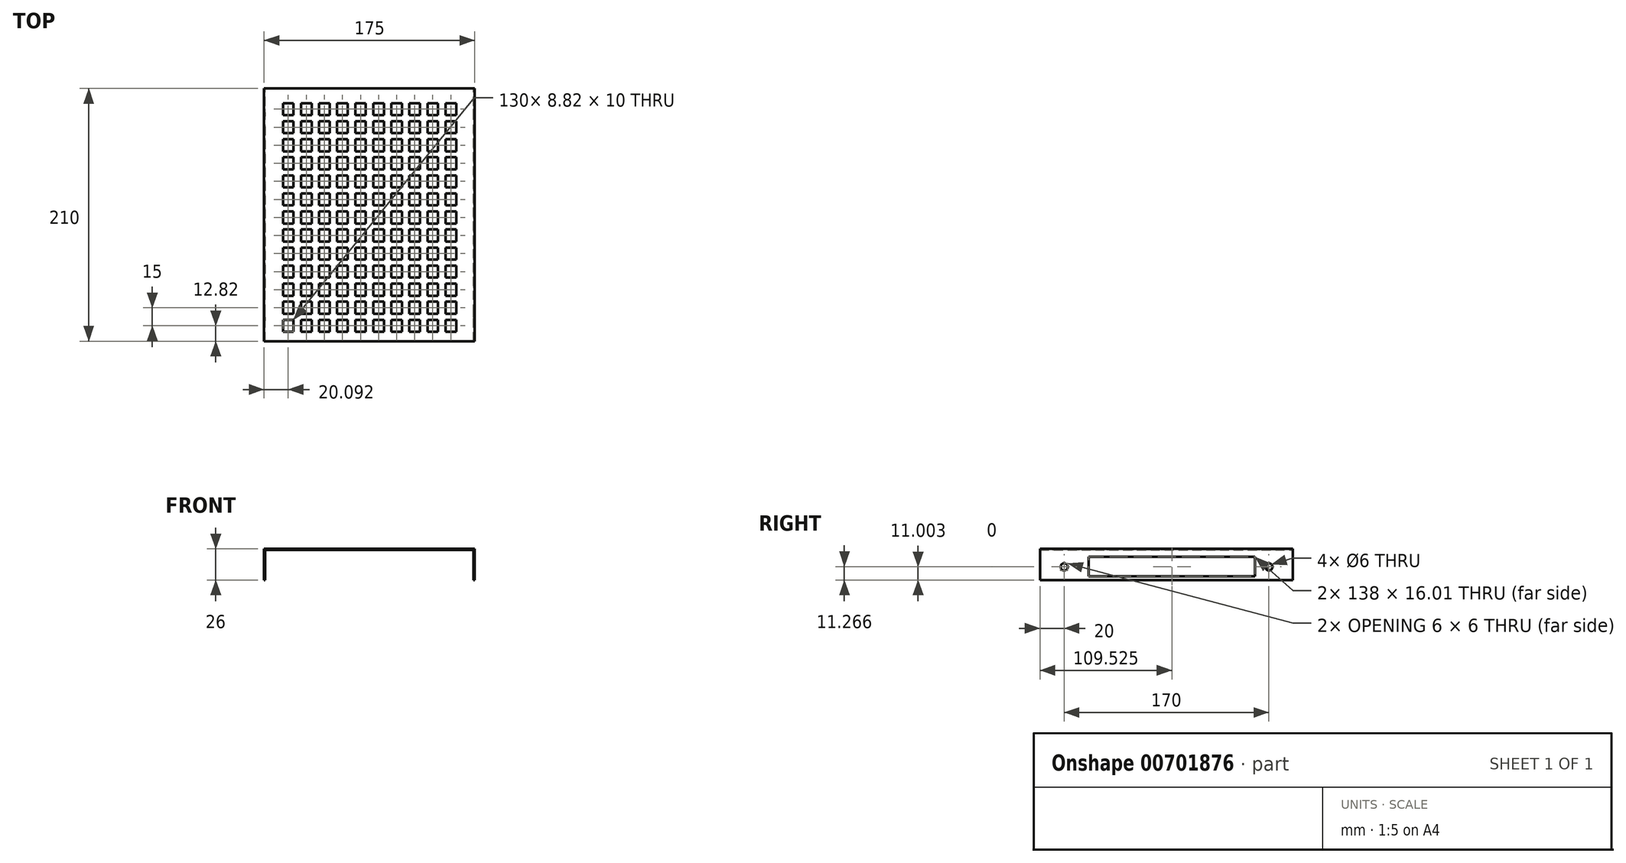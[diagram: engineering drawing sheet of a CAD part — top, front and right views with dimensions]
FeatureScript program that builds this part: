
annotation { "Feature Type Name" : "Feature", "Feature Type Description" : "" }
export const myFeature = defineFeature(function(context is Context, id is Id, definition is map)
    precondition{}
    {
        {
            var Q0;
            Q0=qCreatedBy(makeId("Front.planeOp"),FACE);
            var sketch = newSketch(context, id + "F0", { "sketchPlane" : qUnion([Q0])});
            skLineSegment(sketch, "E0", {"start": v(-108.9, 51.33) * mm, "end": v(66.1, 51.33) * mm});
            skLineSegment(sketch, "E1", {"start": v(-108.9, 51.33) * mm, "end": v(-108.9, 25.33) * mm});
            skLineSegment(sketch, "E2", {"start": v(-108.9, 25.33) * mm, "end": v(-107.9, 25.33) * mm});
            skLineSegment(sketch, "E3", {"start": v(-107.9, 25.33) * mm, "end": v(-107.9, 50.33) * mm});
            skLineSegment(sketch, "E4", {"start": v(66.1, 51.33) * mm, "end": v(66.1, 25.33) * mm});
            skLineSegment(sketch, "E5", {"start": v(66.1, 25.33) * mm, "end": v(65.1, 25.33) * mm});
            skLineSegment(sketch, "E6", {"start": v(65.1, 25.33) * mm, "end": v(65.1, 50.33) * mm});
            skLineSegment(sketch, "E7", {"start": v(65.1, 50.33) * mm, "end": v(-107.9, 50.33) * mm});
            skSolve(sketch);
        }
        {
            var Q0;
            Q0=qSketchRegion(id+"F0",true);
            extrude(context, id + "F1", {"entities" : qUnion([Q0]), "depth" : 210 * mm, "offsetDistance" : 25 * mm});
        }
        {
            var Q0;
            Q0=makeQuery(id+"F1.opExtrude","SWEPT_FACE",FACE,{"disambiguationData":[OSD([sQuery(id+"F0.wireOp",EDGE,"E4")])]});
            var sketch = newSketch(context, id + "F2", { "sketchPlane" : qUnion([Q0])});
            skCircle(sketch, "E8", {"center": v(-190, 36.33) * mm, "radius": 3 * mm});
            skCircle(sketch, "E9", {"center": v(-20, 36.33) * mm, "radius": 3 * mm});
            skSolve(sketch);
        }
        {
            var Q0;
            Q0=sQuery(id+"F2.wireOp",VERTEX,"E8.center");
            var Q1;
            Q1=makeQuery(id+"F1.opExtrude","SWEPT_BODY",BODY,{"disambiguationData":[OSD([sQuery(id+"F0.wireOp",EDGE,"E0"),sQuery(id+"F0.wireOp",EDGE,"E1"),sQuery(id+"F0.wireOp",EDGE,"E2"),sQuery(id+"F0.wireOp",EDGE,"E3"),sQuery(id+"F0.wireOp",EDGE,"E4"),sQuery(id+"F0.wireOp",EDGE,"E5"),sQuery(id+"F0.wireOp",EDGE,"E6"),sQuery(id+"F0.wireOp",EDGE,"E7")])]});
            hole(context, id + "F3", {"style" : HoleStyle.SIMPLE, "endStyle" : HoleEndStyle.THROUGH, "holeDiameter" : 6 * mm, "majorDiameter" : 5 * mm, "isTappedThrough" : true, "tappedDepth" : 12 * mm, "tapClearance" : 3, "locations" : qUnion([Q0]), "scope" : qUnion([Q1])});
        }
        {
            var Q0;
            Q0=sQuery(id+"F2.wireOp",VERTEX,"E9.center");
            var Q1;
            Q1=makeQuery(id+"F1.opExtrude","SWEPT_BODY",BODY,{"disambiguationData":[OSD([sQuery(id+"F0.wireOp",EDGE,"E0"),sQuery(id+"F0.wireOp",EDGE,"E1"),sQuery(id+"F0.wireOp",EDGE,"E2"),sQuery(id+"F0.wireOp",EDGE,"E3"),sQuery(id+"F0.wireOp",EDGE,"E4"),sQuery(id+"F0.wireOp",EDGE,"E5"),sQuery(id+"F0.wireOp",EDGE,"E6"),sQuery(id+"F0.wireOp",EDGE,"E7")])]});
            hole(context, id + "F4", {"style" : HoleStyle.SIMPLE, "endStyle" : HoleEndStyle.THROUGH, "holeDiameter" : 6 * mm, "majorDiameter" : 5 * mm, "isTappedThrough" : true, "tappedDepth" : 12 * mm, "tapClearance" : 3, "locations" : qUnion([Q0]), "scope" : qUnion([Q1])});
        }
        {
            var Q0;
            Q0=qCreatedBy(makeId("Right.planeOp"),FACE);
            var sketch = newSketch(context, id + "F5", { "sketchPlane" : qUnion([Q0])});
            skLineSegment(sketch, "E10.bottom", {"start": v(-169.47, 44.6) * mm, "end": v(-31.48, 44.6) * mm});
            skLineSegment(sketch, "E10.top", {"start": v(-169.47, 28.6) * mm, "end": v(-31.48, 28.6) * mm});
            skLineSegment(sketch, "E10.left", {"start": v(-169.47, 44.6) * mm, "end": v(-169.47, 28.6) * mm});
            skLineSegment(sketch, "E10.right", {"start": v(-31.48, 44.6) * mm, "end": v(-31.48, 28.6) * mm});
            skPoint(sketch, "E10.middle", {"position": v(-100.47, 36.6) * mm});
            skSolve(sketch);
        }
        {
            var Q0;
            Q0=makeQuery(id+"F5.imprint","IMPRINT",FACE,{"disambiguationData":[TD([[makeQuery(id+"F5.imprint","IMPRINT",EDGE,{"derivedFrom":sQuery(id+"F5.wireOp",EDGE,"E10.bottom")}),-1.0]])]});
            extrude(context, id + "F6", {"entities" : qUnion([Q0]), "operationType" : NewBodyOperationType.REMOVE, "endBound" : BoundingType.SYMMETRIC, "oppositeDirection" : true, "depth" : 300 * mm, "offsetDistance" : 25 * mm});
        }
        {
            var Q0;
            Q0=makeQuery(id+"F1.opExtrude","SWEPT_FACE",FACE,{"disambiguationData":[OSD([sQuery(id+"F0.wireOp",EDGE,"E0")])]});
            var sketch = newSketch(context, id + "F7", { "sketchPlane" : qUnion([Q0])});
            skLineSegment(sketch, "E11.bottom", {"start": v(-93.22, -12.18) * mm, "end": v(-84.4, -12.18) * mm});
            skLineSegment(sketch, "E11.top", {"start": v(-93.22, -22.18) * mm, "end": v(-84.4, -22.18) * mm});
            skLineSegment(sketch, "E11.left", {"start": v(-93.22, -12.18) * mm, "end": v(-93.22, -22.18) * mm});
            skLineSegment(sketch, "E11.right", {"start": v(-84.4, -12.18) * mm, "end": v(-84.4, -22.18) * mm});
            skLineSegment(sketch, "E12.0.1.0", {"start": v(-84.4, -27.18) * mm, "end": v(-84.4, -37.18) * mm});
            skLineSegment(sketch, "E12.0.1.1", {"start": v(-93.22, -27.18) * mm, "end": v(-84.4, -27.18) * mm});
            skLineSegment(sketch, "E12.0.1.2", {"start": v(-93.22, -37.18) * mm, "end": v(-84.4, -37.18) * mm});
            skLineSegment(sketch, "E12.0.1.3", {"start": v(-93.22, -27.18) * mm, "end": v(-93.22, -37.18) * mm});
            skLineSegment(sketch, "E12.0.2.0", {"start": v(-84.4, -42.18) * mm, "end": v(-84.4, -52.18) * mm});
            skLineSegment(sketch, "E12.0.2.1", {"start": v(-93.22, -42.18) * mm, "end": v(-84.4, -42.18) * mm});
            skLineSegment(sketch, "E12.0.2.2", {"start": v(-93.22, -52.18) * mm, "end": v(-84.4, -52.18) * mm});
            skLineSegment(sketch, "E12.0.2.3", {"start": v(-93.22, -42.18) * mm, "end": v(-93.22, -52.18) * mm});
            skLineSegment(sketch, "E12.0.3.0", {"start": v(-84.4, -57.18) * mm, "end": v(-84.4, -67.18) * mm});
            skLineSegment(sketch, "E12.0.3.1", {"start": v(-93.22, -57.18) * mm, "end": v(-84.4, -57.18) * mm});
            skLineSegment(sketch, "E12.0.3.2", {"start": v(-93.22, -67.18) * mm, "end": v(-84.4, -67.18) * mm});
            skLineSegment(sketch, "E12.0.3.3", {"start": v(-93.22, -57.18) * mm, "end": v(-93.22, -67.18) * mm});
            skLineSegment(sketch, "E12.0.4.0", {"start": v(-84.4, -72.18) * mm, "end": v(-84.4, -82.18) * mm});
            skLineSegment(sketch, "E12.0.4.1", {"start": v(-93.22, -72.18) * mm, "end": v(-84.4, -72.18) * mm});
            skLineSegment(sketch, "E12.0.4.2", {"start": v(-93.22, -82.18) * mm, "end": v(-84.4, -82.18) * mm});
            skLineSegment(sketch, "E12.0.4.3", {"start": v(-93.22, -72.18) * mm, "end": v(-93.22, -82.18) * mm});
            skLineSegment(sketch, "E12.0.5.0", {"start": v(-84.4, -87.18) * mm, "end": v(-84.4, -97.18) * mm});
            skLineSegment(sketch, "E12.0.5.1", {"start": v(-93.22, -87.18) * mm, "end": v(-84.4, -87.18) * mm});
            skLineSegment(sketch, "E12.0.5.2", {"start": v(-93.22, -97.18) * mm, "end": v(-84.4, -97.18) * mm});
            skLineSegment(sketch, "E12.0.5.3", {"start": v(-93.22, -87.18) * mm, "end": v(-93.22, -97.18) * mm});
            skLineSegment(sketch, "E12.0.6.0", {"start": v(-84.4, -102.18) * mm, "end": v(-84.4, -112.18) * mm});
            skLineSegment(sketch, "E12.0.6.1", {"start": v(-93.22, -102.18) * mm, "end": v(-84.4, -102.18) * mm});
            skLineSegment(sketch, "E12.0.6.2", {"start": v(-93.22, -112.18) * mm, "end": v(-84.4, -112.18) * mm});
            skLineSegment(sketch, "E12.0.6.3", {"start": v(-93.22, -102.18) * mm, "end": v(-93.22, -112.18) * mm});
            skLineSegment(sketch, "E12.0.7.0", {"start": v(-84.4, -117.18) * mm, "end": v(-84.4, -127.18) * mm});
            skLineSegment(sketch, "E12.0.7.1", {"start": v(-93.22, -117.18) * mm, "end": v(-84.4, -117.18) * mm});
            skLineSegment(sketch, "E12.0.7.2", {"start": v(-93.22, -127.18) * mm, "end": v(-84.4, -127.18) * mm});
            skLineSegment(sketch, "E12.0.7.3", {"start": v(-93.22, -117.18) * mm, "end": v(-93.22, -127.18) * mm});
            skLineSegment(sketch, "E12.0.8.0", {"start": v(-84.4, -132.18) * mm, "end": v(-84.4, -142.18) * mm});
            skLineSegment(sketch, "E12.0.8.1", {"start": v(-93.22, -132.18) * mm, "end": v(-84.4, -132.18) * mm});
            skLineSegment(sketch, "E12.0.8.2", {"start": v(-93.22, -142.18) * mm, "end": v(-84.4, -142.18) * mm});
            skLineSegment(sketch, "E12.0.8.3", {"start": v(-93.22, -132.18) * mm, "end": v(-93.22, -142.18) * mm});
            skLineSegment(sketch, "E12.0.9.0", {"start": v(-84.4, -147.18) * mm, "end": v(-84.4, -157.18) * mm});
            skLineSegment(sketch, "E12.0.9.1", {"start": v(-93.22, -147.18) * mm, "end": v(-84.4, -147.18) * mm});
            skLineSegment(sketch, "E12.0.9.2", {"start": v(-93.22, -157.18) * mm, "end": v(-84.4, -157.18) * mm});
            skLineSegment(sketch, "E12.0.9.3", {"start": v(-93.22, -147.18) * mm, "end": v(-93.22, -157.18) * mm});
            skLineSegment(sketch, "E12.1.0.0", {"start": v(-69.4, -12.18) * mm, "end": v(-69.4, -22.18) * mm});
            skLineSegment(sketch, "E12.1.0.1", {"start": v(-78.22, -12.18) * mm, "end": v(-69.4, -12.18) * mm});
            skLineSegment(sketch, "E12.1.0.2", {"start": v(-78.22, -22.18) * mm, "end": v(-69.4, -22.18) * mm});
            skLineSegment(sketch, "E12.1.0.3", {"start": v(-78.22, -12.18) * mm, "end": v(-78.22, -22.18) * mm});
            skLineSegment(sketch, "E12.1.1.0", {"start": v(-69.4, -27.18) * mm, "end": v(-69.4, -37.18) * mm});
            skLineSegment(sketch, "E12.1.1.1", {"start": v(-78.22, -27.18) * mm, "end": v(-69.4, -27.18) * mm});
            skLineSegment(sketch, "E12.1.1.2", {"start": v(-78.22, -37.18) * mm, "end": v(-69.4, -37.18) * mm});
            skLineSegment(sketch, "E12.1.1.3", {"start": v(-78.22, -27.18) * mm, "end": v(-78.22, -37.18) * mm});
            skLineSegment(sketch, "E12.1.2.0", {"start": v(-69.4, -42.18) * mm, "end": v(-69.4, -52.18) * mm});
            skLineSegment(sketch, "E12.1.2.1", {"start": v(-78.22, -42.18) * mm, "end": v(-69.4, -42.18) * mm});
            skLineSegment(sketch, "E12.1.2.2", {"start": v(-78.22, -52.18) * mm, "end": v(-69.4, -52.18) * mm});
            skLineSegment(sketch, "E12.1.2.3", {"start": v(-78.22, -42.18) * mm, "end": v(-78.22, -52.18) * mm});
            skLineSegment(sketch, "E12.1.3.0", {"start": v(-69.4, -57.18) * mm, "end": v(-69.4, -67.18) * mm});
            skLineSegment(sketch, "E12.1.3.1", {"start": v(-78.22, -57.18) * mm, "end": v(-69.4, -57.18) * mm});
            skLineSegment(sketch, "E12.1.3.2", {"start": v(-78.22, -67.18) * mm, "end": v(-69.4, -67.18) * mm});
            skLineSegment(sketch, "E12.1.3.3", {"start": v(-78.22, -57.18) * mm, "end": v(-78.22, -67.18) * mm});
            skLineSegment(sketch, "E12.1.4.0", {"start": v(-69.4, -72.18) * mm, "end": v(-69.4, -82.18) * mm});
            skLineSegment(sketch, "E12.1.4.1", {"start": v(-78.22, -72.18) * mm, "end": v(-69.4, -72.18) * mm});
            skLineSegment(sketch, "E12.1.4.2", {"start": v(-78.22, -82.18) * mm, "end": v(-69.4, -82.18) * mm});
            skLineSegment(sketch, "E12.1.4.3", {"start": v(-78.22, -72.18) * mm, "end": v(-78.22, -82.18) * mm});
            skLineSegment(sketch, "E12.1.5.0", {"start": v(-69.4, -87.18) * mm, "end": v(-69.4, -97.18) * mm});
            skLineSegment(sketch, "E12.1.5.1", {"start": v(-78.22, -87.18) * mm, "end": v(-69.4, -87.18) * mm});
            skLineSegment(sketch, "E12.1.5.2", {"start": v(-78.22, -97.18) * mm, "end": v(-69.4, -97.18) * mm});
            skLineSegment(sketch, "E12.1.5.3", {"start": v(-78.22, -87.18) * mm, "end": v(-78.22, -97.18) * mm});
            skLineSegment(sketch, "E12.1.6.0", {"start": v(-69.4, -102.18) * mm, "end": v(-69.4, -112.18) * mm});
            skLineSegment(sketch, "E12.1.6.1", {"start": v(-78.22, -102.18) * mm, "end": v(-69.4, -102.18) * mm});
            skLineSegment(sketch, "E12.1.6.2", {"start": v(-78.22, -112.18) * mm, "end": v(-69.4, -112.18) * mm});
            skLineSegment(sketch, "E12.1.6.3", {"start": v(-78.22, -102.18) * mm, "end": v(-78.22, -112.18) * mm});
            skLineSegment(sketch, "E12.1.7.0", {"start": v(-69.4, -117.18) * mm, "end": v(-69.4, -127.18) * mm});
            skLineSegment(sketch, "E12.1.7.1", {"start": v(-78.22, -117.18) * mm, "end": v(-69.4, -117.18) * mm});
            skLineSegment(sketch, "E12.1.7.2", {"start": v(-78.22, -127.18) * mm, "end": v(-69.4, -127.18) * mm});
            skLineSegment(sketch, "E12.1.7.3", {"start": v(-78.22, -117.18) * mm, "end": v(-78.22, -127.18) * mm});
            skLineSegment(sketch, "E12.1.8.0", {"start": v(-69.4, -132.18) * mm, "end": v(-69.4, -142.18) * mm});
            skLineSegment(sketch, "E12.1.8.1", {"start": v(-78.22, -132.18) * mm, "end": v(-69.4, -132.18) * mm});
            skLineSegment(sketch, "E12.1.8.2", {"start": v(-78.22, -142.18) * mm, "end": v(-69.4, -142.18) * mm});
            skLineSegment(sketch, "E12.1.8.3", {"start": v(-78.22, -132.18) * mm, "end": v(-78.22, -142.18) * mm});
            skLineSegment(sketch, "E12.1.9.0", {"start": v(-69.4, -147.18) * mm, "end": v(-69.4, -157.18) * mm});
            skLineSegment(sketch, "E12.1.9.1", {"start": v(-78.22, -147.18) * mm, "end": v(-69.4, -147.18) * mm});
            skLineSegment(sketch, "E12.1.9.2", {"start": v(-78.22, -157.18) * mm, "end": v(-69.4, -157.18) * mm});
            skLineSegment(sketch, "E12.1.9.3", {"start": v(-78.22, -147.18) * mm, "end": v(-78.22, -157.18) * mm});
            skLineSegment(sketch, "E12.2.0.0", {"start": v(-54.4, -12.18) * mm, "end": v(-54.4, -22.18) * mm});
            skLineSegment(sketch, "E12.2.0.1", {"start": v(-63.22, -12.18) * mm, "end": v(-54.4, -12.18) * mm});
            skLineSegment(sketch, "E12.2.0.2", {"start": v(-63.22, -22.18) * mm, "end": v(-54.4, -22.18) * mm});
            skLineSegment(sketch, "E12.2.0.3", {"start": v(-63.22, -12.18) * mm, "end": v(-63.22, -22.18) * mm});
            skLineSegment(sketch, "E12.2.1.0", {"start": v(-54.4, -27.18) * mm, "end": v(-54.4, -37.18) * mm});
            skLineSegment(sketch, "E12.2.1.1", {"start": v(-63.22, -27.18) * mm, "end": v(-54.4, -27.18) * mm});
            skLineSegment(sketch, "E12.2.1.2", {"start": v(-63.22, -37.18) * mm, "end": v(-54.4, -37.18) * mm});
            skLineSegment(sketch, "E12.2.1.3", {"start": v(-63.22, -27.18) * mm, "end": v(-63.22, -37.18) * mm});
            skLineSegment(sketch, "E12.2.2.0", {"start": v(-54.4, -42.18) * mm, "end": v(-54.4, -52.18) * mm});
            skLineSegment(sketch, "E12.2.2.1", {"start": v(-63.22, -42.18) * mm, "end": v(-54.4, -42.18) * mm});
            skLineSegment(sketch, "E12.2.2.2", {"start": v(-63.22, -52.18) * mm, "end": v(-54.4, -52.18) * mm});
            skLineSegment(sketch, "E12.2.2.3", {"start": v(-63.22, -42.18) * mm, "end": v(-63.22, -52.18) * mm});
            skLineSegment(sketch, "E12.2.3.0", {"start": v(-54.4, -57.18) * mm, "end": v(-54.4, -67.18) * mm});
            skLineSegment(sketch, "E12.2.3.1", {"start": v(-63.22, -57.18) * mm, "end": v(-54.4, -57.18) * mm});
            skLineSegment(sketch, "E12.2.3.2", {"start": v(-63.22, -67.18) * mm, "end": v(-54.4, -67.18) * mm});
            skLineSegment(sketch, "E12.2.3.3", {"start": v(-63.22, -57.18) * mm, "end": v(-63.22, -67.18) * mm});
            skLineSegment(sketch, "E12.2.4.0", {"start": v(-54.4, -72.18) * mm, "end": v(-54.4, -82.18) * mm});
            skLineSegment(sketch, "E12.2.4.1", {"start": v(-63.22, -72.18) * mm, "end": v(-54.4, -72.18) * mm});
            skLineSegment(sketch, "E12.2.4.2", {"start": v(-63.22, -82.18) * mm, "end": v(-54.4, -82.18) * mm});
            skLineSegment(sketch, "E12.2.4.3", {"start": v(-63.22, -72.18) * mm, "end": v(-63.22, -82.18) * mm});
            skLineSegment(sketch, "E12.2.5.0", {"start": v(-54.4, -87.18) * mm, "end": v(-54.4, -97.18) * mm});
            skLineSegment(sketch, "E12.2.5.1", {"start": v(-63.22, -87.18) * mm, "end": v(-54.4, -87.18) * mm});
            skLineSegment(sketch, "E12.2.5.2", {"start": v(-63.22, -97.18) * mm, "end": v(-54.4, -97.18) * mm});
            skLineSegment(sketch, "E12.2.5.3", {"start": v(-63.22, -87.18) * mm, "end": v(-63.22, -97.18) * mm});
            skLineSegment(sketch, "E12.2.6.0", {"start": v(-54.4, -102.18) * mm, "end": v(-54.4, -112.18) * mm});
            skLineSegment(sketch, "E12.2.6.1", {"start": v(-63.22, -102.18) * mm, "end": v(-54.4, -102.18) * mm});
            skLineSegment(sketch, "E12.2.6.2", {"start": v(-63.22, -112.18) * mm, "end": v(-54.4, -112.18) * mm});
            skLineSegment(sketch, "E12.2.6.3", {"start": v(-63.22, -102.18) * mm, "end": v(-63.22, -112.18) * mm});
            skLineSegment(sketch, "E12.2.7.0", {"start": v(-54.4, -117.18) * mm, "end": v(-54.4, -127.18) * mm});
            skLineSegment(sketch, "E12.2.7.1", {"start": v(-63.22, -117.18) * mm, "end": v(-54.4, -117.18) * mm});
            skLineSegment(sketch, "E12.2.7.2", {"start": v(-63.22, -127.18) * mm, "end": v(-54.4, -127.18) * mm});
            skLineSegment(sketch, "E12.2.7.3", {"start": v(-63.22, -117.18) * mm, "end": v(-63.22, -127.18) * mm});
            skLineSegment(sketch, "E12.2.8.0", {"start": v(-54.4, -132.18) * mm, "end": v(-54.4, -142.18) * mm});
            skLineSegment(sketch, "E12.2.8.1", {"start": v(-63.22, -132.18) * mm, "end": v(-54.4, -132.18) * mm});
            skLineSegment(sketch, "E12.2.8.2", {"start": v(-63.22, -142.18) * mm, "end": v(-54.4, -142.18) * mm});
            skLineSegment(sketch, "E12.2.8.3", {"start": v(-63.22, -132.18) * mm, "end": v(-63.22, -142.18) * mm});
            skLineSegment(sketch, "E12.2.9.0", {"start": v(-54.4, -147.18) * mm, "end": v(-54.4, -157.18) * mm});
            skLineSegment(sketch, "E12.2.9.1", {"start": v(-63.22, -147.18) * mm, "end": v(-54.4, -147.18) * mm});
            skLineSegment(sketch, "E12.2.9.2", {"start": v(-63.22, -157.18) * mm, "end": v(-54.4, -157.18) * mm});
            skLineSegment(sketch, "E12.2.9.3", {"start": v(-63.22, -147.18) * mm, "end": v(-63.22, -157.18) * mm});
            skLineSegment(sketch, "E12.3.0.0", {"start": v(-39.4, -12.18) * mm, "end": v(-39.4, -22.18) * mm});
            skLineSegment(sketch, "E12.3.0.1", {"start": v(-48.22, -12.18) * mm, "end": v(-39.4, -12.18) * mm});
            skLineSegment(sketch, "E12.3.0.2", {"start": v(-48.22, -22.18) * mm, "end": v(-39.4, -22.18) * mm});
            skLineSegment(sketch, "E12.3.0.3", {"start": v(-48.22, -12.18) * mm, "end": v(-48.22, -22.18) * mm});
            skLineSegment(sketch, "E12.3.1.0", {"start": v(-39.4, -27.18) * mm, "end": v(-39.4, -37.18) * mm});
            skLineSegment(sketch, "E12.3.1.1", {"start": v(-48.22, -27.18) * mm, "end": v(-39.4, -27.18) * mm});
            skLineSegment(sketch, "E12.3.1.2", {"start": v(-48.22, -37.18) * mm, "end": v(-39.4, -37.18) * mm});
            skLineSegment(sketch, "E12.3.1.3", {"start": v(-48.22, -27.18) * mm, "end": v(-48.22, -37.18) * mm});
            skLineSegment(sketch, "E12.3.2.0", {"start": v(-39.4, -42.18) * mm, "end": v(-39.4, -52.18) * mm});
            skLineSegment(sketch, "E12.3.2.1", {"start": v(-48.22, -42.18) * mm, "end": v(-39.4, -42.18) * mm});
            skLineSegment(sketch, "E12.3.2.2", {"start": v(-48.22, -52.18) * mm, "end": v(-39.4, -52.18) * mm});
            skLineSegment(sketch, "E12.3.2.3", {"start": v(-48.22, -42.18) * mm, "end": v(-48.22, -52.18) * mm});
            skLineSegment(sketch, "E12.3.3.0", {"start": v(-39.4, -57.18) * mm, "end": v(-39.4, -67.18) * mm});
            skLineSegment(sketch, "E12.3.3.1", {"start": v(-48.22, -57.18) * mm, "end": v(-39.4, -57.18) * mm});
            skLineSegment(sketch, "E12.3.3.2", {"start": v(-48.22, -67.18) * mm, "end": v(-39.4, -67.18) * mm});
            skLineSegment(sketch, "E12.3.3.3", {"start": v(-48.22, -57.18) * mm, "end": v(-48.22, -67.18) * mm});
            skLineSegment(sketch, "E12.3.4.0", {"start": v(-39.4, -72.18) * mm, "end": v(-39.4, -82.18) * mm});
            skLineSegment(sketch, "E12.3.4.1", {"start": v(-48.22, -72.18) * mm, "end": v(-39.4, -72.18) * mm});
            skLineSegment(sketch, "E12.3.4.2", {"start": v(-48.22, -82.18) * mm, "end": v(-39.4, -82.18) * mm});
            skLineSegment(sketch, "E12.3.4.3", {"start": v(-48.22, -72.18) * mm, "end": v(-48.22, -82.18) * mm});
            skLineSegment(sketch, "E12.3.5.0", {"start": v(-39.4, -87.18) * mm, "end": v(-39.4, -97.18) * mm});
            skLineSegment(sketch, "E12.3.5.1", {"start": v(-48.22, -87.18) * mm, "end": v(-39.4, -87.18) * mm});
            skLineSegment(sketch, "E12.3.5.2", {"start": v(-48.22, -97.18) * mm, "end": v(-39.4, -97.18) * mm});
            skLineSegment(sketch, "E12.3.5.3", {"start": v(-48.22, -87.18) * mm, "end": v(-48.22, -97.18) * mm});
            skLineSegment(sketch, "E12.3.6.0", {"start": v(-39.4, -102.18) * mm, "end": v(-39.4, -112.18) * mm});
            skLineSegment(sketch, "E12.3.6.1", {"start": v(-48.22, -102.18) * mm, "end": v(-39.4, -102.18) * mm});
            skLineSegment(sketch, "E12.3.6.2", {"start": v(-48.22, -112.18) * mm, "end": v(-39.4, -112.18) * mm});
            skLineSegment(sketch, "E12.3.6.3", {"start": v(-48.22, -102.18) * mm, "end": v(-48.22, -112.18) * mm});
            skLineSegment(sketch, "E12.3.7.0", {"start": v(-39.4, -117.18) * mm, "end": v(-39.4, -127.18) * mm});
            skLineSegment(sketch, "E12.3.7.1", {"start": v(-48.22, -117.18) * mm, "end": v(-39.4, -117.18) * mm});
            skLineSegment(sketch, "E12.3.7.2", {"start": v(-48.22, -127.18) * mm, "end": v(-39.4, -127.18) * mm});
            skLineSegment(sketch, "E12.3.7.3", {"start": v(-48.22, -117.18) * mm, "end": v(-48.22, -127.18) * mm});
            skLineSegment(sketch, "E12.3.8.0", {"start": v(-39.4, -132.18) * mm, "end": v(-39.4, -142.18) * mm});
            skLineSegment(sketch, "E12.3.8.1", {"start": v(-48.22, -132.18) * mm, "end": v(-39.4, -132.18) * mm});
            skLineSegment(sketch, "E12.3.8.2", {"start": v(-48.22, -142.18) * mm, "end": v(-39.4, -142.18) * mm});
            skLineSegment(sketch, "E12.3.8.3", {"start": v(-48.22, -132.18) * mm, "end": v(-48.22, -142.18) * mm});
            skLineSegment(sketch, "E12.3.9.0", {"start": v(-39.4, -147.18) * mm, "end": v(-39.4, -157.18) * mm});
            skLineSegment(sketch, "E12.3.9.1", {"start": v(-48.22, -147.18) * mm, "end": v(-39.4, -147.18) * mm});
            skLineSegment(sketch, "E12.3.9.2", {"start": v(-48.22, -157.18) * mm, "end": v(-39.4, -157.18) * mm});
            skLineSegment(sketch, "E12.3.9.3", {"start": v(-48.22, -147.18) * mm, "end": v(-48.22, -157.18) * mm});
            skLineSegment(sketch, "E12.4.0.0", {"start": v(-24.4, -12.18) * mm, "end": v(-24.4, -22.18) * mm});
            skLineSegment(sketch, "E12.4.0.1", {"start": v(-33.22, -12.18) * mm, "end": v(-24.4, -12.18) * mm});
            skLineSegment(sketch, "E12.4.0.2", {"start": v(-33.22, -22.18) * mm, "end": v(-24.4, -22.18) * mm});
            skLineSegment(sketch, "E12.4.0.3", {"start": v(-33.22, -12.18) * mm, "end": v(-33.22, -22.18) * mm});
            skLineSegment(sketch, "E12.4.1.0", {"start": v(-24.4, -27.18) * mm, "end": v(-24.4, -37.18) * mm});
            skLineSegment(sketch, "E12.4.1.1", {"start": v(-33.22, -27.18) * mm, "end": v(-24.4, -27.18) * mm});
            skLineSegment(sketch, "E12.4.1.2", {"start": v(-33.22, -37.18) * mm, "end": v(-24.4, -37.18) * mm});
            skLineSegment(sketch, "E12.4.1.3", {"start": v(-33.22, -27.18) * mm, "end": v(-33.22, -37.18) * mm});
            skLineSegment(sketch, "E12.4.2.0", {"start": v(-24.4, -42.18) * mm, "end": v(-24.4, -52.18) * mm});
            skLineSegment(sketch, "E12.4.2.1", {"start": v(-33.22, -42.18) * mm, "end": v(-24.4, -42.18) * mm});
            skLineSegment(sketch, "E12.4.2.2", {"start": v(-33.22, -52.18) * mm, "end": v(-24.4, -52.18) * mm});
            skLineSegment(sketch, "E12.4.2.3", {"start": v(-33.22, -42.18) * mm, "end": v(-33.22, -52.18) * mm});
            skLineSegment(sketch, "E12.4.3.0", {"start": v(-24.4, -57.18) * mm, "end": v(-24.4, -67.18) * mm});
            skLineSegment(sketch, "E12.4.3.1", {"start": v(-33.22, -57.18) * mm, "end": v(-24.4, -57.18) * mm});
            skLineSegment(sketch, "E12.4.3.2", {"start": v(-33.22, -67.18) * mm, "end": v(-24.4, -67.18) * mm});
            skLineSegment(sketch, "E12.4.3.3", {"start": v(-33.22, -57.18) * mm, "end": v(-33.22, -67.18) * mm});
            skLineSegment(sketch, "E12.4.4.0", {"start": v(-24.4, -72.18) * mm, "end": v(-24.4, -82.18) * mm});
            skLineSegment(sketch, "E12.4.4.1", {"start": v(-33.22, -72.18) * mm, "end": v(-24.4, -72.18) * mm});
            skLineSegment(sketch, "E12.4.4.2", {"start": v(-33.22, -82.18) * mm, "end": v(-24.4, -82.18) * mm});
            skLineSegment(sketch, "E12.4.4.3", {"start": v(-33.22, -72.18) * mm, "end": v(-33.22, -82.18) * mm});
            skLineSegment(sketch, "E12.4.5.0", {"start": v(-24.4, -87.18) * mm, "end": v(-24.4, -97.18) * mm});
            skLineSegment(sketch, "E12.4.5.1", {"start": v(-33.22, -87.18) * mm, "end": v(-24.4, -87.18) * mm});
            skLineSegment(sketch, "E12.4.5.2", {"start": v(-33.22, -97.18) * mm, "end": v(-24.4, -97.18) * mm});
            skLineSegment(sketch, "E12.4.5.3", {"start": v(-33.22, -87.18) * mm, "end": v(-33.22, -97.18) * mm});
            skLineSegment(sketch, "E12.4.6.0", {"start": v(-24.4, -102.18) * mm, "end": v(-24.4, -112.18) * mm});
            skLineSegment(sketch, "E12.4.6.1", {"start": v(-33.22, -102.18) * mm, "end": v(-24.4, -102.18) * mm});
            skLineSegment(sketch, "E12.4.6.2", {"start": v(-33.22, -112.18) * mm, "end": v(-24.4, -112.18) * mm});
            skLineSegment(sketch, "E12.4.6.3", {"start": v(-33.22, -102.18) * mm, "end": v(-33.22, -112.18) * mm});
            skLineSegment(sketch, "E12.4.7.0", {"start": v(-24.4, -117.18) * mm, "end": v(-24.4, -127.18) * mm});
            skLineSegment(sketch, "E12.4.7.1", {"start": v(-33.22, -117.18) * mm, "end": v(-24.4, -117.18) * mm});
            skLineSegment(sketch, "E12.4.7.2", {"start": v(-33.22, -127.18) * mm, "end": v(-24.4, -127.18) * mm});
            skLineSegment(sketch, "E12.4.7.3", {"start": v(-33.22, -117.18) * mm, "end": v(-33.22, -127.18) * mm});
            skLineSegment(sketch, "E12.4.8.0", {"start": v(-24.4, -132.18) * mm, "end": v(-24.4, -142.18) * mm});
            skLineSegment(sketch, "E12.4.8.1", {"start": v(-33.22, -132.18) * mm, "end": v(-24.4, -132.18) * mm});
            skLineSegment(sketch, "E12.4.8.2", {"start": v(-33.22, -142.18) * mm, "end": v(-24.4, -142.18) * mm});
            skLineSegment(sketch, "E12.4.8.3", {"start": v(-33.22, -132.18) * mm, "end": v(-33.22, -142.18) * mm});
            skLineSegment(sketch, "E12.4.9.0", {"start": v(-24.4, -147.18) * mm, "end": v(-24.4, -157.18) * mm});
            skLineSegment(sketch, "E12.4.9.1", {"start": v(-33.22, -147.18) * mm, "end": v(-24.4, -147.18) * mm});
            skLineSegment(sketch, "E12.4.9.2", {"start": v(-33.22, -157.18) * mm, "end": v(-24.4, -157.18) * mm});
            skLineSegment(sketch, "E12.4.9.3", {"start": v(-33.22, -147.18) * mm, "end": v(-33.22, -157.18) * mm});
            skLineSegment(sketch, "E12.5.0.0", {"start": v(-9.4, -12.18) * mm, "end": v(-9.4, -22.18) * mm});
            skLineSegment(sketch, "E12.5.0.1", {"start": v(-18.22, -12.18) * mm, "end": v(-9.4, -12.18) * mm});
            skLineSegment(sketch, "E12.5.0.2", {"start": v(-18.22, -22.18) * mm, "end": v(-9.4, -22.18) * mm});
            skLineSegment(sketch, "E12.5.0.3", {"start": v(-18.22, -12.18) * mm, "end": v(-18.22, -22.18) * mm});
            skLineSegment(sketch, "E12.5.1.0", {"start": v(-9.4, -27.18) * mm, "end": v(-9.4, -37.18) * mm});
            skLineSegment(sketch, "E12.5.1.1", {"start": v(-18.22, -27.18) * mm, "end": v(-9.4, -27.18) * mm});
            skLineSegment(sketch, "E12.5.1.2", {"start": v(-18.22, -37.18) * mm, "end": v(-9.4, -37.18) * mm});
            skLineSegment(sketch, "E12.5.1.3", {"start": v(-18.22, -27.18) * mm, "end": v(-18.22, -37.18) * mm});
            skLineSegment(sketch, "E12.5.2.0", {"start": v(-9.4, -42.18) * mm, "end": v(-9.4, -52.18) * mm});
            skLineSegment(sketch, "E12.5.2.1", {"start": v(-18.22, -42.18) * mm, "end": v(-9.4, -42.18) * mm});
            skLineSegment(sketch, "E12.5.2.2", {"start": v(-18.22, -52.18) * mm, "end": v(-9.4, -52.18) * mm});
            skLineSegment(sketch, "E12.5.2.3", {"start": v(-18.22, -42.18) * mm, "end": v(-18.22, -52.18) * mm});
            skLineSegment(sketch, "E12.5.3.0", {"start": v(-9.4, -57.18) * mm, "end": v(-9.4, -67.18) * mm});
            skLineSegment(sketch, "E12.5.3.1", {"start": v(-18.22, -57.18) * mm, "end": v(-9.4, -57.18) * mm});
            skLineSegment(sketch, "E12.5.3.2", {"start": v(-18.22, -67.18) * mm, "end": v(-9.4, -67.18) * mm});
            skLineSegment(sketch, "E12.5.3.3", {"start": v(-18.22, -57.18) * mm, "end": v(-18.22, -67.18) * mm});
            skLineSegment(sketch, "E12.5.4.0", {"start": v(-9.4, -72.18) * mm, "end": v(-9.4, -82.18) * mm});
            skLineSegment(sketch, "E12.5.4.1", {"start": v(-18.22, -72.18) * mm, "end": v(-9.4, -72.18) * mm});
            skLineSegment(sketch, "E12.5.4.2", {"start": v(-18.22, -82.18) * mm, "end": v(-9.4, -82.18) * mm});
            skLineSegment(sketch, "E12.5.4.3", {"start": v(-18.22, -72.18) * mm, "end": v(-18.22, -82.18) * mm});
            skLineSegment(sketch, "E12.5.5.0", {"start": v(-9.4, -87.18) * mm, "end": v(-9.4, -97.18) * mm});
            skLineSegment(sketch, "E12.5.5.1", {"start": v(-18.22, -87.18) * mm, "end": v(-9.4, -87.18) * mm});
            skLineSegment(sketch, "E12.5.5.2", {"start": v(-18.22, -97.18) * mm, "end": v(-9.4, -97.18) * mm});
            skLineSegment(sketch, "E12.5.5.3", {"start": v(-18.22, -87.18) * mm, "end": v(-18.22, -97.18) * mm});
            skLineSegment(sketch, "E12.5.6.0", {"start": v(-9.4, -102.18) * mm, "end": v(-9.4, -112.18) * mm});
            skLineSegment(sketch, "E12.5.6.1", {"start": v(-18.22, -102.18) * mm, "end": v(-9.4, -102.18) * mm});
            skLineSegment(sketch, "E12.5.6.2", {"start": v(-18.22, -112.18) * mm, "end": v(-9.4, -112.18) * mm});
            skLineSegment(sketch, "E12.5.6.3", {"start": v(-18.22, -102.18) * mm, "end": v(-18.22, -112.18) * mm});
            skLineSegment(sketch, "E12.5.7.0", {"start": v(-9.4, -117.18) * mm, "end": v(-9.4, -127.18) * mm});
            skLineSegment(sketch, "E12.5.7.1", {"start": v(-18.22, -117.18) * mm, "end": v(-9.4, -117.18) * mm});
            skLineSegment(sketch, "E12.5.7.2", {"start": v(-18.22, -127.18) * mm, "end": v(-9.4, -127.18) * mm});
            skLineSegment(sketch, "E12.5.7.3", {"start": v(-18.22, -117.18) * mm, "end": v(-18.22, -127.18) * mm});
            skLineSegment(sketch, "E12.5.8.0", {"start": v(-9.4, -132.18) * mm, "end": v(-9.4, -142.18) * mm});
            skLineSegment(sketch, "E12.5.8.1", {"start": v(-18.22, -132.18) * mm, "end": v(-9.4, -132.18) * mm});
            skLineSegment(sketch, "E12.5.8.2", {"start": v(-18.22, -142.18) * mm, "end": v(-9.4, -142.18) * mm});
            skLineSegment(sketch, "E12.5.8.3", {"start": v(-18.22, -132.18) * mm, "end": v(-18.22, -142.18) * mm});
            skLineSegment(sketch, "E12.5.9.0", {"start": v(-9.4, -147.18) * mm, "end": v(-9.4, -157.18) * mm});
            skLineSegment(sketch, "E12.5.9.1", {"start": v(-18.22, -147.18) * mm, "end": v(-9.4, -147.18) * mm});
            skLineSegment(sketch, "E12.5.9.2", {"start": v(-18.22, -157.18) * mm, "end": v(-9.4, -157.18) * mm});
            skLineSegment(sketch, "E12.5.9.3", {"start": v(-18.22, -147.18) * mm, "end": v(-18.22, -157.18) * mm});
            skLineSegment(sketch, "E12.6.0.0", {"start": v(5.6, -12.18) * mm, "end": v(5.6, -22.18) * mm});
            skLineSegment(sketch, "E12.6.0.1", {"start": v(-3.22, -12.18) * mm, "end": v(5.6, -12.18) * mm});
            skLineSegment(sketch, "E12.6.0.2", {"start": v(-3.22, -22.18) * mm, "end": v(5.6, -22.18) * mm});
            skLineSegment(sketch, "E12.6.0.3", {"start": v(-3.22, -12.18) * mm, "end": v(-3.22, -22.18) * mm});
            skLineSegment(sketch, "E12.6.1.0", {"start": v(5.6, -27.18) * mm, "end": v(5.6, -37.18) * mm});
            skLineSegment(sketch, "E12.6.1.1", {"start": v(-3.22, -27.18) * mm, "end": v(5.6, -27.18) * mm});
            skLineSegment(sketch, "E12.6.1.2", {"start": v(-3.22, -37.18) * mm, "end": v(5.6, -37.18) * mm});
            skLineSegment(sketch, "E12.6.1.3", {"start": v(-3.22, -27.18) * mm, "end": v(-3.22, -37.18) * mm});
            skLineSegment(sketch, "E12.6.2.0", {"start": v(5.6, -42.18) * mm, "end": v(5.6, -52.18) * mm});
            skLineSegment(sketch, "E12.6.2.1", {"start": v(-3.22, -42.18) * mm, "end": v(5.6, -42.18) * mm});
            skLineSegment(sketch, "E12.6.2.2", {"start": v(-3.22, -52.18) * mm, "end": v(5.6, -52.18) * mm});
            skLineSegment(sketch, "E12.6.2.3", {"start": v(-3.22, -42.18) * mm, "end": v(-3.22, -52.18) * mm});
            skLineSegment(sketch, "E12.6.3.0", {"start": v(5.6, -57.18) * mm, "end": v(5.6, -67.18) * mm});
            skLineSegment(sketch, "E12.6.3.1", {"start": v(-3.22, -57.18) * mm, "end": v(5.6, -57.18) * mm});
            skLineSegment(sketch, "E12.6.3.2", {"start": v(-3.22, -67.18) * mm, "end": v(5.6, -67.18) * mm});
            skLineSegment(sketch, "E12.6.3.3", {"start": v(-3.22, -57.18) * mm, "end": v(-3.22, -67.18) * mm});
            skLineSegment(sketch, "E12.6.4.0", {"start": v(5.6, -72.18) * mm, "end": v(5.6, -82.18) * mm});
            skLineSegment(sketch, "E12.6.4.1", {"start": v(-3.22, -72.18) * mm, "end": v(5.6, -72.18) * mm});
            skLineSegment(sketch, "E12.6.4.2", {"start": v(-3.22, -82.18) * mm, "end": v(5.6, -82.18) * mm});
            skLineSegment(sketch, "E12.6.4.3", {"start": v(-3.22, -72.18) * mm, "end": v(-3.22, -82.18) * mm});
            skLineSegment(sketch, "E12.6.5.0", {"start": v(5.6, -87.18) * mm, "end": v(5.6, -97.18) * mm});
            skLineSegment(sketch, "E12.6.5.1", {"start": v(-3.22, -87.18) * mm, "end": v(5.6, -87.18) * mm});
            skLineSegment(sketch, "E12.6.5.2", {"start": v(-3.22, -97.18) * mm, "end": v(5.6, -97.18) * mm});
            skLineSegment(sketch, "E12.6.5.3", {"start": v(-3.22, -87.18) * mm, "end": v(-3.22, -97.18) * mm});
            skLineSegment(sketch, "E12.6.6.0", {"start": v(5.6, -102.18) * mm, "end": v(5.6, -112.18) * mm});
            skLineSegment(sketch, "E12.6.6.1", {"start": v(-3.22, -102.18) * mm, "end": v(5.6, -102.18) * mm});
            skLineSegment(sketch, "E12.6.6.2", {"start": v(-3.22, -112.18) * mm, "end": v(5.6, -112.18) * mm});
            skLineSegment(sketch, "E12.6.6.3", {"start": v(-3.22, -102.18) * mm, "end": v(-3.22, -112.18) * mm});
            skLineSegment(sketch, "E12.6.7.0", {"start": v(5.6, -117.18) * mm, "end": v(5.6, -127.18) * mm});
            skLineSegment(sketch, "E12.6.7.1", {"start": v(-3.22, -117.18) * mm, "end": v(5.6, -117.18) * mm});
            skLineSegment(sketch, "E12.6.7.2", {"start": v(-3.22, -127.18) * mm, "end": v(5.6, -127.18) * mm});
            skLineSegment(sketch, "E12.6.7.3", {"start": v(-3.22, -117.18) * mm, "end": v(-3.22, -127.18) * mm});
            skLineSegment(sketch, "E12.6.8.0", {"start": v(5.6, -132.18) * mm, "end": v(5.6, -142.18) * mm});
            skLineSegment(sketch, "E12.6.8.1", {"start": v(-3.22, -132.18) * mm, "end": v(5.6, -132.18) * mm});
            skLineSegment(sketch, "E12.6.8.2", {"start": v(-3.22, -142.18) * mm, "end": v(5.6, -142.18) * mm});
            skLineSegment(sketch, "E12.6.8.3", {"start": v(-3.22, -132.18) * mm, "end": v(-3.22, -142.18) * mm});
            skLineSegment(sketch, "E12.6.9.0", {"start": v(5.6, -147.18) * mm, "end": v(5.6, -157.18) * mm});
            skLineSegment(sketch, "E12.6.9.1", {"start": v(-3.22, -147.18) * mm, "end": v(5.6, -147.18) * mm});
            skLineSegment(sketch, "E12.6.9.2", {"start": v(-3.22, -157.18) * mm, "end": v(5.6, -157.18) * mm});
            skLineSegment(sketch, "E12.6.9.3", {"start": v(-3.22, -147.18) * mm, "end": v(-3.22, -157.18) * mm});
            skLineSegment(sketch, "E12.7.0.0", {"start": v(20.6, -12.18) * mm, "end": v(20.6, -22.18) * mm});
            skLineSegment(sketch, "E12.7.0.1", {"start": v(11.78, -12.18) * mm, "end": v(20.6, -12.18) * mm});
            skLineSegment(sketch, "E12.7.0.2", {"start": v(11.78, -22.18) * mm, "end": v(20.6, -22.18) * mm});
            skLineSegment(sketch, "E12.7.0.3", {"start": v(11.78, -12.18) * mm, "end": v(11.78, -22.18) * mm});
            skLineSegment(sketch, "E12.7.1.0", {"start": v(20.6, -27.18) * mm, "end": v(20.6, -37.18) * mm});
            skLineSegment(sketch, "E12.7.1.1", {"start": v(11.78, -27.18) * mm, "end": v(20.6, -27.18) * mm});
            skLineSegment(sketch, "E12.7.1.2", {"start": v(11.78, -37.18) * mm, "end": v(20.6, -37.18) * mm});
            skLineSegment(sketch, "E12.7.1.3", {"start": v(11.78, -27.18) * mm, "end": v(11.78, -37.18) * mm});
            skLineSegment(sketch, "E12.7.2.0", {"start": v(20.6, -42.18) * mm, "end": v(20.6, -52.18) * mm});
            skLineSegment(sketch, "E12.7.2.1", {"start": v(11.78, -42.18) * mm, "end": v(20.6, -42.18) * mm});
            skLineSegment(sketch, "E12.7.2.2", {"start": v(11.78, -52.18) * mm, "end": v(20.6, -52.18) * mm});
            skLineSegment(sketch, "E12.7.2.3", {"start": v(11.78, -42.18) * mm, "end": v(11.78, -52.18) * mm});
            skLineSegment(sketch, "E12.7.3.0", {"start": v(20.6, -57.18) * mm, "end": v(20.6, -67.18) * mm});
            skLineSegment(sketch, "E12.7.3.1", {"start": v(11.78, -57.18) * mm, "end": v(20.6, -57.18) * mm});
            skLineSegment(sketch, "E12.7.3.2", {"start": v(11.78, -67.18) * mm, "end": v(20.6, -67.18) * mm});
            skLineSegment(sketch, "E12.7.3.3", {"start": v(11.78, -57.18) * mm, "end": v(11.78, -67.18) * mm});
            skLineSegment(sketch, "E12.7.4.0", {"start": v(20.6, -72.18) * mm, "end": v(20.6, -82.18) * mm});
            skLineSegment(sketch, "E12.7.4.1", {"start": v(11.78, -72.18) * mm, "end": v(20.6, -72.18) * mm});
            skLineSegment(sketch, "E12.7.4.2", {"start": v(11.78, -82.18) * mm, "end": v(20.6, -82.18) * mm});
            skLineSegment(sketch, "E12.7.4.3", {"start": v(11.78, -72.18) * mm, "end": v(11.78, -82.18) * mm});
            skLineSegment(sketch, "E12.7.5.0", {"start": v(20.6, -87.18) * mm, "end": v(20.6, -97.18) * mm});
            skLineSegment(sketch, "E12.7.5.1", {"start": v(11.78, -87.18) * mm, "end": v(20.6, -87.18) * mm});
            skLineSegment(sketch, "E12.7.5.2", {"start": v(11.78, -97.18) * mm, "end": v(20.6, -97.18) * mm});
            skLineSegment(sketch, "E12.7.5.3", {"start": v(11.78, -87.18) * mm, "end": v(11.78, -97.18) * mm});
            skLineSegment(sketch, "E12.7.6.0", {"start": v(20.6, -102.18) * mm, "end": v(20.6, -112.18) * mm});
            skLineSegment(sketch, "E12.7.6.1", {"start": v(11.78, -102.18) * mm, "end": v(20.6, -102.18) * mm});
            skLineSegment(sketch, "E12.7.6.2", {"start": v(11.78, -112.18) * mm, "end": v(20.6, -112.18) * mm});
            skLineSegment(sketch, "E12.7.6.3", {"start": v(11.78, -102.18) * mm, "end": v(11.78, -112.18) * mm});
            skLineSegment(sketch, "E12.7.7.0", {"start": v(20.6, -117.18) * mm, "end": v(20.6, -127.18) * mm});
            skLineSegment(sketch, "E12.7.7.1", {"start": v(11.78, -117.18) * mm, "end": v(20.6, -117.18) * mm});
            skLineSegment(sketch, "E12.7.7.2", {"start": v(11.78, -127.18) * mm, "end": v(20.6, -127.18) * mm});
            skLineSegment(sketch, "E12.7.7.3", {"start": v(11.78, -117.18) * mm, "end": v(11.78, -127.18) * mm});
            skLineSegment(sketch, "E12.7.8.0", {"start": v(20.6, -132.18) * mm, "end": v(20.6, -142.18) * mm});
            skLineSegment(sketch, "E12.7.8.1", {"start": v(11.78, -132.18) * mm, "end": v(20.6, -132.18) * mm});
            skLineSegment(sketch, "E12.7.8.2", {"start": v(11.78, -142.18) * mm, "end": v(20.6, -142.18) * mm});
            skLineSegment(sketch, "E12.7.8.3", {"start": v(11.78, -132.18) * mm, "end": v(11.78, -142.18) * mm});
            skLineSegment(sketch, "E12.7.9.0", {"start": v(20.6, -147.18) * mm, "end": v(20.6, -157.18) * mm});
            skLineSegment(sketch, "E12.7.9.1", {"start": v(11.78, -147.18) * mm, "end": v(20.6, -147.18) * mm});
            skLineSegment(sketch, "E12.7.9.2", {"start": v(11.78, -157.18) * mm, "end": v(20.6, -157.18) * mm});
            skLineSegment(sketch, "E12.7.9.3", {"start": v(11.78, -147.18) * mm, "end": v(11.78, -157.18) * mm});
            skLineSegment(sketch, "E12.8.0.0", {"start": v(35.6, -12.18) * mm, "end": v(35.6, -22.18) * mm});
            skLineSegment(sketch, "E12.8.0.1", {"start": v(26.78, -12.18) * mm, "end": v(35.6, -12.18) * mm});
            skLineSegment(sketch, "E12.8.0.2", {"start": v(26.78, -22.18) * mm, "end": v(35.6, -22.18) * mm});
            skLineSegment(sketch, "E12.8.0.3", {"start": v(26.78, -12.18) * mm, "end": v(26.78, -22.18) * mm});
            skLineSegment(sketch, "E12.8.1.0", {"start": v(35.6, -27.18) * mm, "end": v(35.6, -37.18) * mm});
            skLineSegment(sketch, "E12.8.1.1", {"start": v(26.78, -27.18) * mm, "end": v(35.6, -27.18) * mm});
            skLineSegment(sketch, "E12.8.1.2", {"start": v(26.78, -37.18) * mm, "end": v(35.6, -37.18) * mm});
            skLineSegment(sketch, "E12.8.1.3", {"start": v(26.78, -27.18) * mm, "end": v(26.78, -37.18) * mm});
            skLineSegment(sketch, "E12.8.2.0", {"start": v(35.6, -42.18) * mm, "end": v(35.6, -52.18) * mm});
            skLineSegment(sketch, "E12.8.2.1", {"start": v(26.78, -42.18) * mm, "end": v(35.6, -42.18) * mm});
            skLineSegment(sketch, "E12.8.2.2", {"start": v(26.78, -52.18) * mm, "end": v(35.6, -52.18) * mm});
            skLineSegment(sketch, "E12.8.2.3", {"start": v(26.78, -42.18) * mm, "end": v(26.78, -52.18) * mm});
            skLineSegment(sketch, "E12.8.3.0", {"start": v(35.6, -57.18) * mm, "end": v(35.6, -67.18) * mm});
            skLineSegment(sketch, "E12.8.3.1", {"start": v(26.78, -57.18) * mm, "end": v(35.6, -57.18) * mm});
            skLineSegment(sketch, "E12.8.3.2", {"start": v(26.78, -67.18) * mm, "end": v(35.6, -67.18) * mm});
            skLineSegment(sketch, "E12.8.3.3", {"start": v(26.78, -57.18) * mm, "end": v(26.78, -67.18) * mm});
            skLineSegment(sketch, "E12.8.4.0", {"start": v(35.6, -72.18) * mm, "end": v(35.6, -82.18) * mm});
            skLineSegment(sketch, "E12.8.4.1", {"start": v(26.78, -72.18) * mm, "end": v(35.6, -72.18) * mm});
            skLineSegment(sketch, "E12.8.4.2", {"start": v(26.78, -82.18) * mm, "end": v(35.6, -82.18) * mm});
            skLineSegment(sketch, "E12.8.4.3", {"start": v(26.78, -72.18) * mm, "end": v(26.78, -82.18) * mm});
            skLineSegment(sketch, "E12.8.5.0", {"start": v(35.6, -87.18) * mm, "end": v(35.6, -97.18) * mm});
            skLineSegment(sketch, "E12.8.5.1", {"start": v(26.78, -87.18) * mm, "end": v(35.6, -87.18) * mm});
            skLineSegment(sketch, "E12.8.5.2", {"start": v(26.78, -97.18) * mm, "end": v(35.6, -97.18) * mm});
            skLineSegment(sketch, "E12.8.5.3", {"start": v(26.78, -87.18) * mm, "end": v(26.78, -97.18) * mm});
            skLineSegment(sketch, "E12.8.6.0", {"start": v(35.6, -102.18) * mm, "end": v(35.6, -112.18) * mm});
            skLineSegment(sketch, "E12.8.6.1", {"start": v(26.78, -102.18) * mm, "end": v(35.6, -102.18) * mm});
            skLineSegment(sketch, "E12.8.6.2", {"start": v(26.78, -112.18) * mm, "end": v(35.6, -112.18) * mm});
            skLineSegment(sketch, "E12.8.6.3", {"start": v(26.78, -102.18) * mm, "end": v(26.78, -112.18) * mm});
            skLineSegment(sketch, "E12.8.7.0", {"start": v(35.6, -117.18) * mm, "end": v(35.6, -127.18) * mm});
            skLineSegment(sketch, "E12.8.7.1", {"start": v(26.78, -117.18) * mm, "end": v(35.6, -117.18) * mm});
            skLineSegment(sketch, "E12.8.7.2", {"start": v(26.78, -127.18) * mm, "end": v(35.6, -127.18) * mm});
            skLineSegment(sketch, "E12.8.7.3", {"start": v(26.78, -117.18) * mm, "end": v(26.78, -127.18) * mm});
            skLineSegment(sketch, "E12.8.8.0", {"start": v(35.6, -132.18) * mm, "end": v(35.6, -142.18) * mm});
            skLineSegment(sketch, "E12.8.8.1", {"start": v(26.78, -132.18) * mm, "end": v(35.6, -132.18) * mm});
            skLineSegment(sketch, "E12.8.8.2", {"start": v(26.78, -142.18) * mm, "end": v(35.6, -142.18) * mm});
            skLineSegment(sketch, "E12.8.8.3", {"start": v(26.78, -132.18) * mm, "end": v(26.78, -142.18) * mm});
            skLineSegment(sketch, "E12.8.9.0", {"start": v(35.6, -147.18) * mm, "end": v(35.6, -157.18) * mm});
            skLineSegment(sketch, "E12.8.9.1", {"start": v(26.78, -147.18) * mm, "end": v(35.6, -147.18) * mm});
            skLineSegment(sketch, "E12.8.9.2", {"start": v(26.78, -157.18) * mm, "end": v(35.6, -157.18) * mm});
            skLineSegment(sketch, "E12.8.9.3", {"start": v(26.78, -147.18) * mm, "end": v(26.78, -157.18) * mm});
            skLineSegment(sketch, "E12.9.0.0", {"start": v(50.6, -12.18) * mm, "end": v(50.6, -22.18) * mm});
            skLineSegment(sketch, "E12.9.0.1", {"start": v(41.78, -12.18) * mm, "end": v(50.6, -12.18) * mm});
            skLineSegment(sketch, "E12.9.0.2", {"start": v(41.78, -22.18) * mm, "end": v(50.6, -22.18) * mm});
            skLineSegment(sketch, "E12.9.0.3", {"start": v(41.78, -12.18) * mm, "end": v(41.78, -22.18) * mm});
            skLineSegment(sketch, "E12.9.1.0", {"start": v(50.6, -27.18) * mm, "end": v(50.6, -37.18) * mm});
            skLineSegment(sketch, "E12.9.1.1", {"start": v(41.78, -27.18) * mm, "end": v(50.6, -27.18) * mm});
            skLineSegment(sketch, "E12.9.1.2", {"start": v(41.78, -37.18) * mm, "end": v(50.6, -37.18) * mm});
            skLineSegment(sketch, "E12.9.1.3", {"start": v(41.78, -27.18) * mm, "end": v(41.78, -37.18) * mm});
            skLineSegment(sketch, "E12.9.2.0", {"start": v(50.6, -42.18) * mm, "end": v(50.6, -52.18) * mm});
            skLineSegment(sketch, "E12.9.2.1", {"start": v(41.78, -42.18) * mm, "end": v(50.6, -42.18) * mm});
            skLineSegment(sketch, "E12.9.2.2", {"start": v(41.78, -52.18) * mm, "end": v(50.6, -52.18) * mm});
            skLineSegment(sketch, "E12.9.2.3", {"start": v(41.78, -42.18) * mm, "end": v(41.78, -52.18) * mm});
            skLineSegment(sketch, "E12.9.3.0", {"start": v(50.6, -57.18) * mm, "end": v(50.6, -67.18) * mm});
            skLineSegment(sketch, "E12.9.3.1", {"start": v(41.78, -57.18) * mm, "end": v(50.6, -57.18) * mm});
            skLineSegment(sketch, "E12.9.3.2", {"start": v(41.78, -67.18) * mm, "end": v(50.6, -67.18) * mm});
            skLineSegment(sketch, "E12.9.3.3", {"start": v(41.78, -57.18) * mm, "end": v(41.78, -67.18) * mm});
            skLineSegment(sketch, "E12.9.4.0", {"start": v(50.6, -72.18) * mm, "end": v(50.6, -82.18) * mm});
            skLineSegment(sketch, "E12.9.4.1", {"start": v(41.78, -72.18) * mm, "end": v(50.6, -72.18) * mm});
            skLineSegment(sketch, "E12.9.4.2", {"start": v(41.78, -82.18) * mm, "end": v(50.6, -82.18) * mm});
            skLineSegment(sketch, "E12.9.4.3", {"start": v(41.78, -72.18) * mm, "end": v(41.78, -82.18) * mm});
            skLineSegment(sketch, "E12.9.5.0", {"start": v(50.6, -87.18) * mm, "end": v(50.6, -97.18) * mm});
            skLineSegment(sketch, "E12.9.5.1", {"start": v(41.78, -87.18) * mm, "end": v(50.6, -87.18) * mm});
            skLineSegment(sketch, "E12.9.5.2", {"start": v(41.78, -97.18) * mm, "end": v(50.6, -97.18) * mm});
            skLineSegment(sketch, "E12.9.5.3", {"start": v(41.78, -87.18) * mm, "end": v(41.78, -97.18) * mm});
            skLineSegment(sketch, "E12.9.6.0", {"start": v(50.6, -102.18) * mm, "end": v(50.6, -112.18) * mm});
            skLineSegment(sketch, "E12.9.6.1", {"start": v(41.78, -102.18) * mm, "end": v(50.6, -102.18) * mm});
            skLineSegment(sketch, "E12.9.6.2", {"start": v(41.78, -112.18) * mm, "end": v(50.6, -112.18) * mm});
            skLineSegment(sketch, "E12.9.6.3", {"start": v(41.78, -102.18) * mm, "end": v(41.78, -112.18) * mm});
            skLineSegment(sketch, "E12.9.7.0", {"start": v(50.6, -117.18) * mm, "end": v(50.6, -127.18) * mm});
            skLineSegment(sketch, "E12.9.7.1", {"start": v(41.78, -117.18) * mm, "end": v(50.6, -117.18) * mm});
            skLineSegment(sketch, "E12.9.7.2", {"start": v(41.78, -127.18) * mm, "end": v(50.6, -127.18) * mm});
            skLineSegment(sketch, "E12.9.7.3", {"start": v(41.78, -117.18) * mm, "end": v(41.78, -127.18) * mm});
            skLineSegment(sketch, "E12.9.8.0", {"start": v(50.6, -132.18) * mm, "end": v(50.6, -142.18) * mm});
            skLineSegment(sketch, "E12.9.8.1", {"start": v(41.78, -132.18) * mm, "end": v(50.6, -132.18) * mm});
            skLineSegment(sketch, "E12.9.8.2", {"start": v(41.78, -142.18) * mm, "end": v(50.6, -142.18) * mm});
            skLineSegment(sketch, "E12.9.8.3", {"start": v(41.78, -132.18) * mm, "end": v(41.78, -142.18) * mm});
            skLineSegment(sketch, "E12.9.9.0", {"start": v(50.6, -147.18) * mm, "end": v(50.6, -157.18) * mm});
            skLineSegment(sketch, "E12.9.9.1", {"start": v(41.78, -147.18) * mm, "end": v(50.6, -147.18) * mm});
            skLineSegment(sketch, "E12.9.9.2", {"start": v(41.78, -157.18) * mm, "end": v(50.6, -157.18) * mm});
            skLineSegment(sketch, "E12.9.9.3", {"start": v(41.78, -147.18) * mm, "end": v(41.78, -157.18) * mm});
            skLineSegment(sketch, "E12.direction1", {"start": v(-93.22, -22.18) * mm, "end": v(-78.22, -22.18) * mm, "construction": true});
            skLineSegment(sketch, "E12.direction2", {"start": v(-93.22, -22.18) * mm, "end": v(-93.22, -37.18) * mm, "construction": true});
            skLineSegment(sketch, "E13.0.1.0", {"start": v(-93.22, -162.18) * mm, "end": v(-84.4, -162.18) * mm});
            skLineSegment(sketch, "E13.0.1.1", {"start": v(-84.4, -162.18) * mm, "end": v(-84.4, -172.18) * mm});
            skLineSegment(sketch, "E13.0.1.2", {"start": v(-93.22, -162.18) * mm, "end": v(-93.22, -172.18) * mm});
            skLineSegment(sketch, "E13.0.1.3", {"start": v(-93.22, -172.18) * mm, "end": v(-84.4, -172.18) * mm});
            skLineSegment(sketch, "E13.0.2.0", {"start": v(-93.22, -177.18) * mm, "end": v(-84.4, -177.18) * mm});
            skLineSegment(sketch, "E13.0.2.1", {"start": v(-84.4, -177.18) * mm, "end": v(-84.4, -187.18) * mm});
            skLineSegment(sketch, "E13.0.2.2", {"start": v(-93.22, -177.18) * mm, "end": v(-93.22, -187.18) * mm});
            skLineSegment(sketch, "E13.0.2.3", {"start": v(-93.22, -187.18) * mm, "end": v(-84.4, -187.18) * mm});
            skLineSegment(sketch, "E13.0.3.0", {"start": v(-93.22, -192.18) * mm, "end": v(-84.4, -192.18) * mm});
            skLineSegment(sketch, "E13.0.3.1", {"start": v(-84.4, -192.18) * mm, "end": v(-84.4, -202.18) * mm});
            skLineSegment(sketch, "E13.0.3.2", {"start": v(-93.22, -192.18) * mm, "end": v(-93.22, -202.18) * mm});
            skLineSegment(sketch, "E13.0.3.3", {"start": v(-93.22, -202.18) * mm, "end": v(-84.4, -202.18) * mm});
            skLineSegment(sketch, "E13.1.1.0", {"start": v(-78.22, -162.18) * mm, "end": v(-69.4, -162.18) * mm});
            skLineSegment(sketch, "E13.1.1.1", {"start": v(-69.4, -162.18) * mm, "end": v(-69.4, -172.18) * mm});
            skLineSegment(sketch, "E13.1.1.2", {"start": v(-78.22, -162.18) * mm, "end": v(-78.22, -172.18) * mm});
            skLineSegment(sketch, "E13.1.1.3", {"start": v(-78.22, -172.18) * mm, "end": v(-69.4, -172.18) * mm});
            skLineSegment(sketch, "E13.1.2.0", {"start": v(-78.22, -177.18) * mm, "end": v(-69.4, -177.18) * mm});
            skLineSegment(sketch, "E13.1.2.1", {"start": v(-69.4, -177.18) * mm, "end": v(-69.4, -187.18) * mm});
            skLineSegment(sketch, "E13.1.2.2", {"start": v(-78.22, -177.18) * mm, "end": v(-78.22, -187.18) * mm});
            skLineSegment(sketch, "E13.1.2.3", {"start": v(-78.22, -187.18) * mm, "end": v(-69.4, -187.18) * mm});
            skLineSegment(sketch, "E13.1.3.0", {"start": v(-78.22, -192.18) * mm, "end": v(-69.4, -192.18) * mm});
            skLineSegment(sketch, "E13.1.3.1", {"start": v(-69.4, -192.18) * mm, "end": v(-69.4, -202.18) * mm});
            skLineSegment(sketch, "E13.1.3.2", {"start": v(-78.22, -192.18) * mm, "end": v(-78.22, -202.18) * mm});
            skLineSegment(sketch, "E13.1.3.3", {"start": v(-78.22, -202.18) * mm, "end": v(-69.4, -202.18) * mm});
            skLineSegment(sketch, "E13.2.1.0", {"start": v(-63.22, -162.18) * mm, "end": v(-54.4, -162.18) * mm});
            skLineSegment(sketch, "E13.2.1.1", {"start": v(-54.4, -162.18) * mm, "end": v(-54.4, -172.18) * mm});
            skLineSegment(sketch, "E13.2.1.2", {"start": v(-63.22, -162.18) * mm, "end": v(-63.22, -172.18) * mm});
            skLineSegment(sketch, "E13.2.1.3", {"start": v(-63.22, -172.18) * mm, "end": v(-54.4, -172.18) * mm});
            skLineSegment(sketch, "E13.2.2.0", {"start": v(-63.22, -177.18) * mm, "end": v(-54.4, -177.18) * mm});
            skLineSegment(sketch, "E13.2.2.1", {"start": v(-54.4, -177.18) * mm, "end": v(-54.4, -187.18) * mm});
            skLineSegment(sketch, "E13.2.2.2", {"start": v(-63.22, -177.18) * mm, "end": v(-63.22, -187.18) * mm});
            skLineSegment(sketch, "E13.2.2.3", {"start": v(-63.22, -187.18) * mm, "end": v(-54.4, -187.18) * mm});
            skLineSegment(sketch, "E13.2.3.0", {"start": v(-63.22, -192.18) * mm, "end": v(-54.4, -192.18) * mm});
            skLineSegment(sketch, "E13.2.3.1", {"start": v(-54.4, -192.18) * mm, "end": v(-54.4, -202.18) * mm});
            skLineSegment(sketch, "E13.2.3.2", {"start": v(-63.22, -192.18) * mm, "end": v(-63.22, -202.18) * mm});
            skLineSegment(sketch, "E13.2.3.3", {"start": v(-63.22, -202.18) * mm, "end": v(-54.4, -202.18) * mm});
            skLineSegment(sketch, "E13.3.1.0", {"start": v(-48.22, -162.18) * mm, "end": v(-39.4, -162.18) * mm});
            skLineSegment(sketch, "E13.3.1.1", {"start": v(-39.4, -162.18) * mm, "end": v(-39.4, -172.18) * mm});
            skLineSegment(sketch, "E13.3.1.2", {"start": v(-48.22, -162.18) * mm, "end": v(-48.22, -172.18) * mm});
            skLineSegment(sketch, "E13.3.1.3", {"start": v(-48.22, -172.18) * mm, "end": v(-39.4, -172.18) * mm});
            skLineSegment(sketch, "E13.3.2.0", {"start": v(-48.22, -177.18) * mm, "end": v(-39.4, -177.18) * mm});
            skLineSegment(sketch, "E13.3.2.1", {"start": v(-39.4, -177.18) * mm, "end": v(-39.4, -187.18) * mm});
            skLineSegment(sketch, "E13.3.2.2", {"start": v(-48.22, -177.18) * mm, "end": v(-48.22, -187.18) * mm});
            skLineSegment(sketch, "E13.3.2.3", {"start": v(-48.22, -187.18) * mm, "end": v(-39.4, -187.18) * mm});
            skLineSegment(sketch, "E13.3.3.0", {"start": v(-48.22, -192.18) * mm, "end": v(-39.4, -192.18) * mm});
            skLineSegment(sketch, "E13.3.3.1", {"start": v(-39.4, -192.18) * mm, "end": v(-39.4, -202.18) * mm});
            skLineSegment(sketch, "E13.3.3.2", {"start": v(-48.22, -192.18) * mm, "end": v(-48.22, -202.18) * mm});
            skLineSegment(sketch, "E13.3.3.3", {"start": v(-48.22, -202.18) * mm, "end": v(-39.4, -202.18) * mm});
            skLineSegment(sketch, "E13.4.1.0", {"start": v(-33.22, -162.18) * mm, "end": v(-24.4, -162.18) * mm});
            skLineSegment(sketch, "E13.4.1.1", {"start": v(-24.4, -162.18) * mm, "end": v(-24.4, -172.18) * mm});
            skLineSegment(sketch, "E13.4.1.2", {"start": v(-33.22, -162.18) * mm, "end": v(-33.22, -172.18) * mm});
            skLineSegment(sketch, "E13.4.1.3", {"start": v(-33.22, -172.18) * mm, "end": v(-24.4, -172.18) * mm});
            skLineSegment(sketch, "E13.4.2.0", {"start": v(-33.22, -177.18) * mm, "end": v(-24.4, -177.18) * mm});
            skLineSegment(sketch, "E13.4.2.1", {"start": v(-24.4, -177.18) * mm, "end": v(-24.4, -187.18) * mm});
            skLineSegment(sketch, "E13.4.2.2", {"start": v(-33.22, -177.18) * mm, "end": v(-33.22, -187.18) * mm});
            skLineSegment(sketch, "E13.4.2.3", {"start": v(-33.22, -187.18) * mm, "end": v(-24.4, -187.18) * mm});
            skLineSegment(sketch, "E13.4.3.0", {"start": v(-33.22, -192.18) * mm, "end": v(-24.4, -192.18) * mm});
            skLineSegment(sketch, "E13.4.3.1", {"start": v(-24.4, -192.18) * mm, "end": v(-24.4, -202.18) * mm});
            skLineSegment(sketch, "E13.4.3.2", {"start": v(-33.22, -192.18) * mm, "end": v(-33.22, -202.18) * mm});
            skLineSegment(sketch, "E13.4.3.3", {"start": v(-33.22, -202.18) * mm, "end": v(-24.4, -202.18) * mm});
            skLineSegment(sketch, "E13.5.1.0", {"start": v(-18.22, -162.18) * mm, "end": v(-9.4, -162.18) * mm});
            skLineSegment(sketch, "E13.5.1.1", {"start": v(-9.4, -162.18) * mm, "end": v(-9.4, -172.18) * mm});
            skLineSegment(sketch, "E13.5.1.2", {"start": v(-18.22, -162.18) * mm, "end": v(-18.22, -172.18) * mm});
            skLineSegment(sketch, "E13.5.1.3", {"start": v(-18.22, -172.18) * mm, "end": v(-9.4, -172.18) * mm});
            skLineSegment(sketch, "E13.5.2.0", {"start": v(-18.22, -177.18) * mm, "end": v(-9.4, -177.18) * mm});
            skLineSegment(sketch, "E13.5.2.1", {"start": v(-9.4, -177.18) * mm, "end": v(-9.4, -187.18) * mm});
            skLineSegment(sketch, "E13.5.2.2", {"start": v(-18.22, -177.18) * mm, "end": v(-18.22, -187.18) * mm});
            skLineSegment(sketch, "E13.5.2.3", {"start": v(-18.22, -187.18) * mm, "end": v(-9.4, -187.18) * mm});
            skLineSegment(sketch, "E13.5.3.0", {"start": v(-18.22, -192.18) * mm, "end": v(-9.4, -192.18) * mm});
            skLineSegment(sketch, "E13.5.3.1", {"start": v(-9.4, -192.18) * mm, "end": v(-9.4, -202.18) * mm});
            skLineSegment(sketch, "E13.5.3.2", {"start": v(-18.22, -192.18) * mm, "end": v(-18.22, -202.18) * mm});
            skLineSegment(sketch, "E13.5.3.3", {"start": v(-18.22, -202.18) * mm, "end": v(-9.4, -202.18) * mm});
            skLineSegment(sketch, "E13.6.1.0", {"start": v(-3.22, -162.18) * mm, "end": v(5.6, -162.18) * mm});
            skLineSegment(sketch, "E13.6.1.1", {"start": v(5.6, -162.18) * mm, "end": v(5.6, -172.18) * mm});
            skLineSegment(sketch, "E13.6.1.2", {"start": v(-3.22, -162.18) * mm, "end": v(-3.22, -172.18) * mm});
            skLineSegment(sketch, "E13.6.1.3", {"start": v(-3.22, -172.18) * mm, "end": v(5.6, -172.18) * mm});
            skLineSegment(sketch, "E13.6.2.0", {"start": v(-3.22, -177.18) * mm, "end": v(5.6, -177.18) * mm});
            skLineSegment(sketch, "E13.6.2.1", {"start": v(5.6, -177.18) * mm, "end": v(5.6, -187.18) * mm});
            skLineSegment(sketch, "E13.6.2.2", {"start": v(-3.22, -177.18) * mm, "end": v(-3.22, -187.18) * mm});
            skLineSegment(sketch, "E13.6.2.3", {"start": v(-3.22, -187.18) * mm, "end": v(5.6, -187.18) * mm});
            skLineSegment(sketch, "E13.6.3.0", {"start": v(-3.22, -192.18) * mm, "end": v(5.6, -192.18) * mm});
            skLineSegment(sketch, "E13.6.3.1", {"start": v(5.6, -192.18) * mm, "end": v(5.6, -202.18) * mm});
            skLineSegment(sketch, "E13.6.3.2", {"start": v(-3.22, -192.18) * mm, "end": v(-3.22, -202.18) * mm});
            skLineSegment(sketch, "E13.6.3.3", {"start": v(-3.22, -202.18) * mm, "end": v(5.6, -202.18) * mm});
            skLineSegment(sketch, "E13.7.1.0", {"start": v(11.78, -162.18) * mm, "end": v(20.6, -162.18) * mm});
            skLineSegment(sketch, "E13.7.1.1", {"start": v(20.6, -162.18) * mm, "end": v(20.6, -172.18) * mm});
            skLineSegment(sketch, "E13.7.1.2", {"start": v(11.78, -162.18) * mm, "end": v(11.78, -172.18) * mm});
            skLineSegment(sketch, "E13.7.1.3", {"start": v(11.78, -172.18) * mm, "end": v(20.6, -172.18) * mm});
            skLineSegment(sketch, "E13.7.2.0", {"start": v(11.78, -177.18) * mm, "end": v(20.6, -177.18) * mm});
            skLineSegment(sketch, "E13.7.2.1", {"start": v(20.6, -177.18) * mm, "end": v(20.6, -187.18) * mm});
            skLineSegment(sketch, "E13.7.2.2", {"start": v(11.78, -177.18) * mm, "end": v(11.78, -187.18) * mm});
            skLineSegment(sketch, "E13.7.2.3", {"start": v(11.78, -187.18) * mm, "end": v(20.6, -187.18) * mm});
            skLineSegment(sketch, "E13.7.3.0", {"start": v(11.78, -192.18) * mm, "end": v(20.6, -192.18) * mm});
            skLineSegment(sketch, "E13.7.3.1", {"start": v(20.6, -192.18) * mm, "end": v(20.6, -202.18) * mm});
            skLineSegment(sketch, "E13.7.3.2", {"start": v(11.78, -192.18) * mm, "end": v(11.78, -202.18) * mm});
            skLineSegment(sketch, "E13.7.3.3", {"start": v(11.78, -202.18) * mm, "end": v(20.6, -202.18) * mm});
            skLineSegment(sketch, "E13.8.1.0", {"start": v(26.78, -162.18) * mm, "end": v(35.6, -162.18) * mm});
            skLineSegment(sketch, "E13.8.1.1", {"start": v(35.6, -162.18) * mm, "end": v(35.6, -172.18) * mm});
            skLineSegment(sketch, "E13.8.1.2", {"start": v(26.78, -162.18) * mm, "end": v(26.78, -172.18) * mm});
            skLineSegment(sketch, "E13.8.1.3", {"start": v(26.78, -172.18) * mm, "end": v(35.6, -172.18) * mm});
            skLineSegment(sketch, "E13.8.2.0", {"start": v(26.78, -177.18) * mm, "end": v(35.6, -177.18) * mm});
            skLineSegment(sketch, "E13.8.2.1", {"start": v(35.6, -177.18) * mm, "end": v(35.6, -187.18) * mm});
            skLineSegment(sketch, "E13.8.2.2", {"start": v(26.78, -177.18) * mm, "end": v(26.78, -187.18) * mm});
            skLineSegment(sketch, "E13.8.2.3", {"start": v(26.78, -187.18) * mm, "end": v(35.6, -187.18) * mm});
            skLineSegment(sketch, "E13.8.3.0", {"start": v(26.78, -192.18) * mm, "end": v(35.6, -192.18) * mm});
            skLineSegment(sketch, "E13.8.3.1", {"start": v(35.6, -192.18) * mm, "end": v(35.6, -202.18) * mm});
            skLineSegment(sketch, "E13.8.3.2", {"start": v(26.78, -192.18) * mm, "end": v(26.78, -202.18) * mm});
            skLineSegment(sketch, "E13.8.3.3", {"start": v(26.78, -202.18) * mm, "end": v(35.6, -202.18) * mm});
            skLineSegment(sketch, "E13.9.1.0", {"start": v(41.78, -162.18) * mm, "end": v(50.6, -162.18) * mm});
            skLineSegment(sketch, "E13.9.1.1", {"start": v(50.6, -162.18) * mm, "end": v(50.6, -172.18) * mm});
            skLineSegment(sketch, "E13.9.1.2", {"start": v(41.78, -162.18) * mm, "end": v(41.78, -172.18) * mm});
            skLineSegment(sketch, "E13.9.1.3", {"start": v(41.78, -172.18) * mm, "end": v(50.6, -172.18) * mm});
            skLineSegment(sketch, "E13.9.2.0", {"start": v(41.78, -177.18) * mm, "end": v(50.6, -177.18) * mm});
            skLineSegment(sketch, "E13.9.2.1", {"start": v(50.6, -177.18) * mm, "end": v(50.6, -187.18) * mm});
            skLineSegment(sketch, "E13.9.2.2", {"start": v(41.78, -177.18) * mm, "end": v(41.78, -187.18) * mm});
            skLineSegment(sketch, "E13.9.2.3", {"start": v(41.78, -187.18) * mm, "end": v(50.6, -187.18) * mm});
            skLineSegment(sketch, "E13.9.3.0", {"start": v(41.78, -192.18) * mm, "end": v(50.6, -192.18) * mm});
            skLineSegment(sketch, "E13.9.3.1", {"start": v(50.6, -192.18) * mm, "end": v(50.6, -202.18) * mm});
            skLineSegment(sketch, "E13.9.3.2", {"start": v(41.78, -192.18) * mm, "end": v(41.78, -202.18) * mm});
            skLineSegment(sketch, "E13.9.3.3", {"start": v(41.78, -202.18) * mm, "end": v(50.6, -202.18) * mm});
            skLineSegment(sketch, "E13.direction1", {"start": v(-93.22, -157.18) * mm, "end": v(-78.22, -157.18) * mm, "construction": true});
            skLineSegment(sketch, "E13.direction2", {"start": v(-93.22, -157.18) * mm, "end": v(-93.22, -172.18) * mm, "construction": true});
            skSolve(sketch);
        }
        {
            var Q0;
            Q0=makeQuery(id+"F7.imprint","IMPRINT",FACE,{"disambiguationData":[TD([[makeQuery(id+"F7.imprint","IMPRINT",EDGE,{"derivedFrom":sQuery(id+"F7.wireOp",EDGE,"E12.1.0.0")}),-1.0]])]});
            var Q1;
            Q1=makeQuery(id+"F7.imprint","IMPRINT",FACE,{"disambiguationData":[TD([[makeQuery(id+"F7.imprint","IMPRINT",EDGE,{"derivedFrom":sQuery(id+"F7.wireOp",EDGE,"E12.2.0.0")}),-1.0]])]});
            var Q2;
            Q2=makeQuery(id+"F7.imprint","IMPRINT",FACE,{"disambiguationData":[TD([[makeQuery(id+"F7.imprint","IMPRINT",EDGE,{"derivedFrom":sQuery(id+"F7.wireOp",EDGE,"E12.3.0.0")}),-1.0]])]});
            var Q3;
            Q3=makeQuery(id+"F7.imprint","IMPRINT",FACE,{"disambiguationData":[TD([[makeQuery(id+"F7.imprint","IMPRINT",EDGE,{"derivedFrom":sQuery(id+"F7.wireOp",EDGE,"E12.4.0.0")}),-1.0]])]});
            var Q4;
            Q4=makeQuery(id+"F7.imprint","IMPRINT",FACE,{"disambiguationData":[TD([[makeQuery(id+"F7.imprint","IMPRINT",EDGE,{"derivedFrom":sQuery(id+"F7.wireOp",EDGE,"E12.5.0.0")}),-1.0]])]});
            var Q5;
            Q5=makeQuery(id+"F7.imprint","IMPRINT",FACE,{"disambiguationData":[TD([[makeQuery(id+"F7.imprint","IMPRINT",EDGE,{"derivedFrom":sQuery(id+"F7.wireOp",EDGE,"E12.6.0.0")}),-1.0]])]});
            var Q6;
            Q6=makeQuery(id+"F7.imprint","IMPRINT",FACE,{"disambiguationData":[TD([[makeQuery(id+"F7.imprint","IMPRINT",EDGE,{"derivedFrom":sQuery(id+"F7.wireOp",EDGE,"E12.7.0.0")}),-1.0]])]});
            var Q7;
            Q7=makeQuery(id+"F7.imprint","IMPRINT",FACE,{"disambiguationData":[TD([[makeQuery(id+"F7.imprint","IMPRINT",EDGE,{"derivedFrom":sQuery(id+"F7.wireOp",EDGE,"E12.9.0.0")}),-1.0]])]});
            var Q8;
            Q8=makeQuery(id+"F7.imprint","IMPRINT",FACE,{"disambiguationData":[TD([[makeQuery(id+"F7.imprint","IMPRINT",EDGE,{"derivedFrom":sQuery(id+"F7.wireOp",EDGE,"E12.8.0.0")}),-1.0]])]});
            var Q9;
            Q9=makeQuery(id+"F7.imprint","IMPRINT",FACE,{"disambiguationData":[TD([[makeQuery(id+"F7.imprint","IMPRINT",EDGE,{"derivedFrom":sQuery(id+"F7.wireOp",EDGE,"E12.0.1.0")}),-1.0]])]});
            var Q10;
            Q10=makeQuery(id+"F7.imprint","IMPRINT",FACE,{"disambiguationData":[TD([[makeQuery(id+"F7.imprint","IMPRINT",EDGE,{"derivedFrom":sQuery(id+"F7.wireOp",EDGE,"E11.bottom")}),-1.0]])]});
            var Q11;
            Q11=makeQuery(id+"F7.imprint","IMPRINT",FACE,{"disambiguationData":[TD([[makeQuery(id+"F7.imprint","IMPRINT",EDGE,{"derivedFrom":sQuery(id+"F7.wireOp",EDGE,"E12.1.1.0")}),-1.0]])]});
            var Q12;
            Q12=makeQuery(id+"F7.imprint","IMPRINT",FACE,{"disambiguationData":[TD([[makeQuery(id+"F7.imprint","IMPRINT",EDGE,{"derivedFrom":sQuery(id+"F7.wireOp",EDGE,"E12.1.2.0")}),-1.0]])]});
            var Q13;
            Q13=makeQuery(id+"F7.imprint","IMPRINT",FACE,{"disambiguationData":[TD([[makeQuery(id+"F7.imprint","IMPRINT",EDGE,{"derivedFrom":sQuery(id+"F7.wireOp",EDGE,"E12.0.2.0")}),-1.0]])]});
            var Q14;
            Q14=makeQuery(id+"F7.imprint","IMPRINT",FACE,{"disambiguationData":[TD([[makeQuery(id+"F7.imprint","IMPRINT",EDGE,{"derivedFrom":sQuery(id+"F7.wireOp",EDGE,"E12.0.3.0")}),-1.0]])]});
            var Q15;
            Q15=makeQuery(id+"F7.imprint","IMPRINT",FACE,{"disambiguationData":[TD([[makeQuery(id+"F7.imprint","IMPRINT",EDGE,{"derivedFrom":sQuery(id+"F7.wireOp",EDGE,"E12.1.3.0")}),-1.0]])]});
            var Q16;
            Q16=makeQuery(id+"F7.imprint","IMPRINT",FACE,{"disambiguationData":[TD([[makeQuery(id+"F7.imprint","IMPRINT",EDGE,{"derivedFrom":sQuery(id+"F7.wireOp",EDGE,"E12.1.4.0")}),-1.0]])]});
            var Q17;
            Q17=makeQuery(id+"F7.imprint","IMPRINT",FACE,{"disambiguationData":[TD([[makeQuery(id+"F7.imprint","IMPRINT",EDGE,{"derivedFrom":sQuery(id+"F7.wireOp",EDGE,"E12.0.4.0")}),-1.0]])]});
            var Q18;
            Q18=makeQuery(id+"F7.imprint","IMPRINT",FACE,{"disambiguationData":[TD([[makeQuery(id+"F7.imprint","IMPRINT",EDGE,{"derivedFrom":sQuery(id+"F7.wireOp",EDGE,"E12.0.5.0")}),-1.0]])]});
            var Q19;
            Q19=makeQuery(id+"F7.imprint","IMPRINT",FACE,{"disambiguationData":[TD([[makeQuery(id+"F7.imprint","IMPRINT",EDGE,{"derivedFrom":sQuery(id+"F7.wireOp",EDGE,"E12.1.5.0")}),-1.0]])]});
            var Q20;
            Q20=makeQuery(id+"F7.imprint","IMPRINT",FACE,{"disambiguationData":[TD([[makeQuery(id+"F7.imprint","IMPRINT",EDGE,{"derivedFrom":sQuery(id+"F7.wireOp",EDGE,"E12.1.6.0")}),-1.0]])]});
            var Q21;
            Q21=makeQuery(id+"F7.imprint","IMPRINT",FACE,{"disambiguationData":[TD([[makeQuery(id+"F7.imprint","IMPRINT",EDGE,{"derivedFrom":sQuery(id+"F7.wireOp",EDGE,"E12.0.6.0")}),-1.0]])]});
            var Q22;
            Q22=makeQuery(id+"F7.imprint","IMPRINT",FACE,{"disambiguationData":[TD([[makeQuery(id+"F7.imprint","IMPRINT",EDGE,{"derivedFrom":sQuery(id+"F7.wireOp",EDGE,"E12.0.7.0")}),-1.0]])]});
            var Q23;
            Q23=makeQuery(id+"F7.imprint","IMPRINT",FACE,{"disambiguationData":[TD([[makeQuery(id+"F7.imprint","IMPRINT",EDGE,{"derivedFrom":sQuery(id+"F7.wireOp",EDGE,"E12.1.7.0")}),-1.0]])]});
            var Q24;
            Q24=makeQuery(id+"F7.imprint","IMPRINT",FACE,{"disambiguationData":[TD([[makeQuery(id+"F7.imprint","IMPRINT",EDGE,{"derivedFrom":sQuery(id+"F7.wireOp",EDGE,"E12.1.8.0")}),-1.0]])]});
            var Q25;
            Q25=makeQuery(id+"F7.imprint","IMPRINT",FACE,{"disambiguationData":[TD([[makeQuery(id+"F7.imprint","IMPRINT",EDGE,{"derivedFrom":sQuery(id+"F7.wireOp",EDGE,"E12.0.8.0")}),-1.0]])]});
            var Q26;
            Q26=makeQuery(id+"F7.imprint","IMPRINT",FACE,{"disambiguationData":[TD([[makeQuery(id+"F7.imprint","IMPRINT",EDGE,{"derivedFrom":sQuery(id+"F7.wireOp",EDGE,"E12.0.9.0")}),-1.0]])]});
            var Q27;
            Q27=makeQuery(id+"F7.imprint","IMPRINT",FACE,{"disambiguationData":[TD([[makeQuery(id+"F7.imprint","IMPRINT",EDGE,{"derivedFrom":sQuery(id+"F7.wireOp",EDGE,"E12.1.9.1")}),-1.0]])]});
            var Q28;
            Q28=makeQuery(id+"F7.imprint","IMPRINT",FACE,{"disambiguationData":[TD([[makeQuery(id+"F7.imprint","IMPRINT",EDGE,{"derivedFrom":sQuery(id+"F7.wireOp",EDGE,"E13.1.1.0")}),-1.0]])]});
            var Q29;
            Q29=makeQuery(id+"F7.imprint","IMPRINT",FACE,{"disambiguationData":[TD([[makeQuery(id+"F7.imprint","IMPRINT",EDGE,{"derivedFrom":sQuery(id+"F7.wireOp",EDGE,"E13.0.1.0")}),-1.0]])]});
            var Q30;
            Q30=makeQuery(id+"F7.imprint","IMPRINT",FACE,{"disambiguationData":[TD([[makeQuery(id+"F7.imprint","IMPRINT",EDGE,{"derivedFrom":sQuery(id+"F7.wireOp",EDGE,"E13.0.2.0")}),-1.0]])]});
            var Q31;
            Q31=makeQuery(id+"F7.imprint","IMPRINT",FACE,{"disambiguationData":[TD([[makeQuery(id+"F7.imprint","IMPRINT",EDGE,{"derivedFrom":sQuery(id+"F7.wireOp",EDGE,"E13.1.2.0")}),-1.0]])]});
            var Q32;
            Q32=makeQuery(id+"F7.imprint","IMPRINT",FACE,{"disambiguationData":[TD([[makeQuery(id+"F7.imprint","IMPRINT",EDGE,{"derivedFrom":sQuery(id+"F7.wireOp",EDGE,"E13.0.3.0")}),-1.0]])]});
            var Q33;
            Q33=makeQuery(id+"F7.imprint","IMPRINT",FACE,{"disambiguationData":[TD([[makeQuery(id+"F7.imprint","IMPRINT",EDGE,{"derivedFrom":sQuery(id+"F7.wireOp",EDGE,"E13.1.3.0")}),-1.0]])]});
            var Q34;
            Q34=makeQuery(id+"F7.imprint","IMPRINT",FACE,{"disambiguationData":[TD([[makeQuery(id+"F7.imprint","IMPRINT",EDGE,{"derivedFrom":sQuery(id+"F7.wireOp",EDGE,"E12.2.1.0")}),-1.0]])]});
            var Q35;
            Q35=makeQuery(id+"F7.imprint","IMPRINT",FACE,{"disambiguationData":[TD([[makeQuery(id+"F7.imprint","IMPRINT",EDGE,{"derivedFrom":sQuery(id+"F7.wireOp",EDGE,"E12.2.2.0")}),-1.0]])]});
            var Q36;
            Q36=makeQuery(id+"F7.imprint","IMPRINT",FACE,{"disambiguationData":[TD([[makeQuery(id+"F7.imprint","IMPRINT",EDGE,{"derivedFrom":sQuery(id+"F7.wireOp",EDGE,"E12.2.3.0")}),-1.0]])]});
            var Q37;
            Q37=makeQuery(id+"F7.imprint","IMPRINT",FACE,{"disambiguationData":[TD([[makeQuery(id+"F7.imprint","IMPRINT",EDGE,{"derivedFrom":sQuery(id+"F7.wireOp",EDGE,"E12.2.4.0")}),-1.0]])]});
            var Q38;
            Q38=makeQuery(id+"F7.imprint","IMPRINT",FACE,{"disambiguationData":[TD([[makeQuery(id+"F7.imprint","IMPRINT",EDGE,{"derivedFrom":sQuery(id+"F7.wireOp",EDGE,"E12.2.6.0")}),-1.0]])]});
            var Q39;
            Q39=makeQuery(id+"F7.imprint","IMPRINT",FACE,{"disambiguationData":[TD([[makeQuery(id+"F7.imprint","IMPRINT",EDGE,{"derivedFrom":sQuery(id+"F7.wireOp",EDGE,"E12.2.5.0")}),-1.0]])]});
            var Q40;
            Q40=makeQuery(id+"F7.imprint","IMPRINT",FACE,{"disambiguationData":[TD([[makeQuery(id+"F7.imprint","IMPRINT",EDGE,{"derivedFrom":sQuery(id+"F7.wireOp",EDGE,"E12.2.7.0")}),-1.0]])]});
            var Q41;
            Q41=makeQuery(id+"F7.imprint","IMPRINT",FACE,{"disambiguationData":[TD([[makeQuery(id+"F7.imprint","IMPRINT",EDGE,{"derivedFrom":sQuery(id+"F7.wireOp",EDGE,"E12.2.8.0")}),-1.0]])]});
            var Q42;
            Q42=makeQuery(id+"F7.imprint","IMPRINT",FACE,{"disambiguationData":[TD([[makeQuery(id+"F7.imprint","IMPRINT",EDGE,{"derivedFrom":sQuery(id+"F7.wireOp",EDGE,"E12.2.9.1")}),-1.0]])]});
            var Q43;
            Q43=makeQuery(id+"F7.imprint","IMPRINT",FACE,{"disambiguationData":[TD([[makeQuery(id+"F7.imprint","IMPRINT",EDGE,{"derivedFrom":sQuery(id+"F7.wireOp",EDGE,"E13.2.1.0")}),-1.0]])]});
            var Q44;
            Q44=makeQuery(id+"F7.imprint","IMPRINT",FACE,{"disambiguationData":[TD([[makeQuery(id+"F7.imprint","IMPRINT",EDGE,{"derivedFrom":sQuery(id+"F7.wireOp",EDGE,"E13.2.2.0")}),-1.0]])]});
            var Q45;
            Q45=makeQuery(id+"F7.imprint","IMPRINT",FACE,{"disambiguationData":[TD([[makeQuery(id+"F7.imprint","IMPRINT",EDGE,{"derivedFrom":sQuery(id+"F7.wireOp",EDGE,"E13.2.3.0")}),-1.0]])]});
            var Q46;
            Q46=makeQuery(id+"F7.imprint","IMPRINT",FACE,{"disambiguationData":[TD([[makeQuery(id+"F7.imprint","IMPRINT",EDGE,{"derivedFrom":sQuery(id+"F7.wireOp",EDGE,"E13.3.3.0")}),-1.0]])]});
            var Q47;
            Q47=makeQuery(id+"F7.imprint","IMPRINT",FACE,{"disambiguationData":[TD([[makeQuery(id+"F7.imprint","IMPRINT",EDGE,{"derivedFrom":sQuery(id+"F7.wireOp",EDGE,"E13.3.2.0")}),-1.0]])]});
            var Q48;
            Q48=makeQuery(id+"F7.imprint","IMPRINT",FACE,{"disambiguationData":[TD([[makeQuery(id+"F7.imprint","IMPRINT",EDGE,{"derivedFrom":sQuery(id+"F7.wireOp",EDGE,"E12.9.1.0")}),-1.0]])]});
            var Q49;
            Q49=makeQuery(id+"F7.imprint","IMPRINT",FACE,{"disambiguationData":[TD([[makeQuery(id+"F7.imprint","IMPRINT",EDGE,{"derivedFrom":sQuery(id+"F7.wireOp",EDGE,"E12.8.1.0")}),-1.0]])]});
            var Q50;
            Q50=makeQuery(id+"F7.imprint","IMPRINT",FACE,{"disambiguationData":[TD([[makeQuery(id+"F7.imprint","IMPRINT",EDGE,{"derivedFrom":sQuery(id+"F7.wireOp",EDGE,"E12.7.1.0")}),-1.0]])]});
            var Q51;
            Q51=makeQuery(id+"F7.imprint","IMPRINT",FACE,{"disambiguationData":[TD([[makeQuery(id+"F7.imprint","IMPRINT",EDGE,{"derivedFrom":sQuery(id+"F7.wireOp",EDGE,"E12.6.1.0")}),-1.0]])]});
            var Q52;
            Q52=makeQuery(id+"F7.imprint","IMPRINT",FACE,{"disambiguationData":[TD([[makeQuery(id+"F7.imprint","IMPRINT",EDGE,{"derivedFrom":sQuery(id+"F7.wireOp",EDGE,"E12.4.1.0")}),-1.0]])]});
            var Q53;
            Q53=makeQuery(id+"F7.imprint","IMPRINT",FACE,{"disambiguationData":[TD([[makeQuery(id+"F7.imprint","IMPRINT",EDGE,{"derivedFrom":sQuery(id+"F7.wireOp",EDGE,"E12.3.1.0")}),-1.0]])]});
            var Q54;
            Q54=makeQuery(id+"F7.imprint","IMPRINT",FACE,{"disambiguationData":[TD([[makeQuery(id+"F7.imprint","IMPRINT",EDGE,{"derivedFrom":sQuery(id+"F7.wireOp",EDGE,"E12.5.1.0")}),-1.0]])]});
            var Q55;
            Q55=makeQuery(id+"F7.imprint","IMPRINT",FACE,{"disambiguationData":[TD([[makeQuery(id+"F7.imprint","IMPRINT",EDGE,{"derivedFrom":sQuery(id+"F7.wireOp",EDGE,"E12.9.2.0")}),-1.0]])]});
            var Q56;
            Q56=makeQuery(id+"F7.imprint","IMPRINT",FACE,{"disambiguationData":[TD([[makeQuery(id+"F7.imprint","IMPRINT",EDGE,{"derivedFrom":sQuery(id+"F7.wireOp",EDGE,"E12.8.2.0")}),-1.0]])]});
            var Q57;
            Q57=makeQuery(id+"F7.imprint","IMPRINT",FACE,{"disambiguationData":[TD([[makeQuery(id+"F7.imprint","IMPRINT",EDGE,{"derivedFrom":sQuery(id+"F7.wireOp",EDGE,"E12.7.2.0")}),-1.0]])]});
            var Q58;
            Q58=makeQuery(id+"F7.imprint","IMPRINT",FACE,{"disambiguationData":[TD([[makeQuery(id+"F7.imprint","IMPRINT",EDGE,{"derivedFrom":sQuery(id+"F7.wireOp",EDGE,"E12.6.2.0")}),-1.0]])]});
            var Q59;
            Q59=makeQuery(id+"F7.imprint","IMPRINT",FACE,{"disambiguationData":[TD([[makeQuery(id+"F7.imprint","IMPRINT",EDGE,{"derivedFrom":sQuery(id+"F7.wireOp",EDGE,"E12.5.2.0")}),-1.0]])]});
            var Q60;
            Q60=makeQuery(id+"F7.imprint","IMPRINT",FACE,{"disambiguationData":[TD([[makeQuery(id+"F7.imprint","IMPRINT",EDGE,{"derivedFrom":sQuery(id+"F7.wireOp",EDGE,"E12.4.2.0")}),-1.0]])]});
            var Q61;
            Q61=makeQuery(id+"F7.imprint","IMPRINT",FACE,{"disambiguationData":[TD([[makeQuery(id+"F7.imprint","IMPRINT",EDGE,{"derivedFrom":sQuery(id+"F7.wireOp",EDGE,"E12.3.2.0")}),-1.0]])]});
            var Q62;
            Q62=makeQuery(id+"F7.imprint","IMPRINT",FACE,{"disambiguationData":[TD([[makeQuery(id+"F7.imprint","IMPRINT",EDGE,{"derivedFrom":sQuery(id+"F7.wireOp",EDGE,"E12.3.3.0")}),-1.0]])]});
            var Q63;
            Q63=makeQuery(id+"F7.imprint","IMPRINT",FACE,{"disambiguationData":[TD([[makeQuery(id+"F7.imprint","IMPRINT",EDGE,{"derivedFrom":sQuery(id+"F7.wireOp",EDGE,"E12.3.4.0")}),-1.0]])]});
            var Q64;
            Q64=makeQuery(id+"F7.imprint","IMPRINT",FACE,{"disambiguationData":[TD([[makeQuery(id+"F7.imprint","IMPRINT",EDGE,{"derivedFrom":sQuery(id+"F7.wireOp",EDGE,"E12.3.5.0")}),-1.0]])]});
            var Q65;
            Q65=makeQuery(id+"F7.imprint","IMPRINT",FACE,{"disambiguationData":[TD([[makeQuery(id+"F7.imprint","IMPRINT",EDGE,{"derivedFrom":sQuery(id+"F7.wireOp",EDGE,"E12.3.6.0")}),-1.0]])]});
            var Q66;
            Q66=makeQuery(id+"F7.imprint","IMPRINT",FACE,{"disambiguationData":[TD([[makeQuery(id+"F7.imprint","IMPRINT",EDGE,{"derivedFrom":sQuery(id+"F7.wireOp",EDGE,"E12.3.7.0")}),-1.0]])]});
            var Q67;
            Q67=makeQuery(id+"F7.imprint","IMPRINT",FACE,{"disambiguationData":[TD([[makeQuery(id+"F7.imprint","IMPRINT",EDGE,{"derivedFrom":sQuery(id+"F7.wireOp",EDGE,"E12.3.8.0")}),-1.0]])]});
            var Q68;
            Q68=makeQuery(id+"F7.imprint","IMPRINT",FACE,{"disambiguationData":[TD([[makeQuery(id+"F7.imprint","IMPRINT",EDGE,{"derivedFrom":sQuery(id+"F7.wireOp",EDGE,"E12.3.9.1")}),-1.0]])]});
            var Q69;
            Q69=makeQuery(id+"F7.imprint","IMPRINT",FACE,{"disambiguationData":[TD([[makeQuery(id+"F7.imprint","IMPRINT",EDGE,{"derivedFrom":sQuery(id+"F7.wireOp",EDGE,"E13.3.1.0")}),-1.0]])]});
            var Q70;
            Q70=makeQuery(id+"F7.imprint","IMPRINT",FACE,{"disambiguationData":[TD([[makeQuery(id+"F7.imprint","IMPRINT",EDGE,{"derivedFrom":sQuery(id+"F7.wireOp",EDGE,"E13.4.3.0")}),-1.0]])]});
            var Q71;
            Q71=makeQuery(id+"F7.imprint","IMPRINT",FACE,{"disambiguationData":[TD([[makeQuery(id+"F7.imprint","IMPRINT",EDGE,{"derivedFrom":sQuery(id+"F7.wireOp",EDGE,"E13.4.2.0")}),-1.0]])]});
            var Q72;
            Q72=makeQuery(id+"F7.imprint","IMPRINT",FACE,{"disambiguationData":[TD([[makeQuery(id+"F7.imprint","IMPRINT",EDGE,{"derivedFrom":sQuery(id+"F7.wireOp",EDGE,"E13.4.1.0")}),-1.0]])]});
            var Q73;
            Q73=makeQuery(id+"F7.imprint","IMPRINT",FACE,{"disambiguationData":[TD([[makeQuery(id+"F7.imprint","IMPRINT",EDGE,{"derivedFrom":sQuery(id+"F7.wireOp",EDGE,"E12.4.8.0")}),-1.0]])]});
            var Q74;
            Q74=makeQuery(id+"F7.imprint","IMPRINT",FACE,{"disambiguationData":[TD([[makeQuery(id+"F7.imprint","IMPRINT",EDGE,{"derivedFrom":sQuery(id+"F7.wireOp",EDGE,"E12.4.7.0")}),-1.0]])]});
            var Q75;
            Q75=makeQuery(id+"F7.imprint","IMPRINT",FACE,{"disambiguationData":[TD([[makeQuery(id+"F7.imprint","IMPRINT",EDGE,{"derivedFrom":sQuery(id+"F7.wireOp",EDGE,"E12.4.6.0")}),-1.0]])]});
            var Q76;
            Q76=makeQuery(id+"F7.imprint","IMPRINT",FACE,{"disambiguationData":[TD([[makeQuery(id+"F7.imprint","IMPRINT",EDGE,{"derivedFrom":sQuery(id+"F7.wireOp",EDGE,"E12.4.5.0")}),-1.0]])]});
            var Q77;
            Q77=makeQuery(id+"F7.imprint","IMPRINT",FACE,{"disambiguationData":[TD([[makeQuery(id+"F7.imprint","IMPRINT",EDGE,{"derivedFrom":sQuery(id+"F7.wireOp",EDGE,"E12.4.4.0")}),-1.0]])]});
            var Q78;
            Q78=makeQuery(id+"F7.imprint","IMPRINT",FACE,{"disambiguationData":[TD([[makeQuery(id+"F7.imprint","IMPRINT",EDGE,{"derivedFrom":sQuery(id+"F7.wireOp",EDGE,"E12.4.3.0")}),-1.0]])]});
            var Q79;
            Q79=makeQuery(id+"F7.imprint","IMPRINT",FACE,{"disambiguationData":[TD([[makeQuery(id+"F7.imprint","IMPRINT",EDGE,{"derivedFrom":sQuery(id+"F7.wireOp",EDGE,"E12.5.3.0")}),-1.0]])]});
            var Q80;
            Q80=makeQuery(id+"F7.imprint","IMPRINT",FACE,{"disambiguationData":[TD([[makeQuery(id+"F7.imprint","IMPRINT",EDGE,{"derivedFrom":sQuery(id+"F7.wireOp",EDGE,"E12.5.4.0")}),-1.0]])]});
            var Q81;
            Q81=makeQuery(id+"F7.imprint","IMPRINT",FACE,{"disambiguationData":[TD([[makeQuery(id+"F7.imprint","IMPRINT",EDGE,{"derivedFrom":sQuery(id+"F7.wireOp",EDGE,"E12.5.5.0")}),-1.0]])]});
            var Q82;
            Q82=makeQuery(id+"F7.imprint","IMPRINT",FACE,{"disambiguationData":[TD([[makeQuery(id+"F7.imprint","IMPRINT",EDGE,{"derivedFrom":sQuery(id+"F7.wireOp",EDGE,"E12.5.6.0")}),-1.0]])]});
            var Q83;
            Q83=makeQuery(id+"F7.imprint","IMPRINT",FACE,{"disambiguationData":[TD([[makeQuery(id+"F7.imprint","IMPRINT",EDGE,{"derivedFrom":sQuery(id+"F7.wireOp",EDGE,"E12.5.7.0")}),-1.0]])]});
            var Q84;
            Q84=makeQuery(id+"F7.imprint","IMPRINT",FACE,{"disambiguationData":[TD([[makeQuery(id+"F7.imprint","IMPRINT",EDGE,{"derivedFrom":sQuery(id+"F7.wireOp",EDGE,"E12.5.8.0")}),-1.0]])]});
            var Q85;
            Q85=makeQuery(id+"F7.imprint","IMPRINT",FACE,{"disambiguationData":[TD([[makeQuery(id+"F7.imprint","IMPRINT",EDGE,{"derivedFrom":sQuery(id+"F7.wireOp",EDGE,"E12.4.9.1")}),-1.0]])]});
            var Q86;
            Q86=makeQuery(id+"F7.imprint","IMPRINT",FACE,{"disambiguationData":[TD([[makeQuery(id+"F7.imprint","IMPRINT",EDGE,{"derivedFrom":sQuery(id+"F7.wireOp",EDGE,"E12.5.9.1")}),-1.0]])]});
            var Q87;
            Q87=makeQuery(id+"F7.imprint","IMPRINT",FACE,{"disambiguationData":[TD([[makeQuery(id+"F7.imprint","IMPRINT",EDGE,{"derivedFrom":sQuery(id+"F7.wireOp",EDGE,"E13.5.1.0")}),-1.0]])]});
            var Q88;
            Q88=makeQuery(id+"F7.imprint","IMPRINT",FACE,{"disambiguationData":[TD([[makeQuery(id+"F7.imprint","IMPRINT",EDGE,{"derivedFrom":sQuery(id+"F7.wireOp",EDGE,"E13.5.2.0")}),-1.0]])]});
            var Q89;
            Q89=makeQuery(id+"F7.imprint","IMPRINT",FACE,{"disambiguationData":[TD([[makeQuery(id+"F7.imprint","IMPRINT",EDGE,{"derivedFrom":sQuery(id+"F7.wireOp",EDGE,"E13.5.3.0")}),-1.0]])]});
            var Q90;
            Q90=makeQuery(id+"F7.imprint","IMPRINT",FACE,{"disambiguationData":[TD([[makeQuery(id+"F7.imprint","IMPRINT",EDGE,{"derivedFrom":sQuery(id+"F7.wireOp",EDGE,"E13.6.3.0")}),-1.0]])]});
            var Q91;
            Q91=makeQuery(id+"F7.imprint","IMPRINT",FACE,{"disambiguationData":[TD([[makeQuery(id+"F7.imprint","IMPRINT",EDGE,{"derivedFrom":sQuery(id+"F7.wireOp",EDGE,"E13.6.2.0")}),-1.0]])]});
            var Q92;
            Q92=makeQuery(id+"F7.imprint","IMPRINT",FACE,{"disambiguationData":[TD([[makeQuery(id+"F7.imprint","IMPRINT",EDGE,{"derivedFrom":sQuery(id+"F7.wireOp",EDGE,"E13.6.1.0")}),-1.0]])]});
            var Q93;
            Q93=makeQuery(id+"F7.imprint","IMPRINT",FACE,{"disambiguationData":[TD([[makeQuery(id+"F7.imprint","IMPRINT",EDGE,{"derivedFrom":sQuery(id+"F7.wireOp",EDGE,"E12.6.9.1")}),-1.0]])]});
            var Q94;
            Q94=makeQuery(id+"F7.imprint","IMPRINT",FACE,{"disambiguationData":[TD([[makeQuery(id+"F7.imprint","IMPRINT",EDGE,{"derivedFrom":sQuery(id+"F7.wireOp",EDGE,"E12.6.8.0")}),-1.0]])]});
            var Q95;
            Q95=makeQuery(id+"F7.imprint","IMPRINT",FACE,{"disambiguationData":[TD([[makeQuery(id+"F7.imprint","IMPRINT",EDGE,{"derivedFrom":sQuery(id+"F7.wireOp",EDGE,"E12.6.7.0")}),-1.0]])]});
            var Q96;
            Q96=makeQuery(id+"F7.imprint","IMPRINT",FACE,{"disambiguationData":[TD([[makeQuery(id+"F7.imprint","IMPRINT",EDGE,{"derivedFrom":sQuery(id+"F7.wireOp",EDGE,"E12.6.6.0")}),-1.0]])]});
            var Q97;
            Q97=makeQuery(id+"F7.imprint","IMPRINT",FACE,{"disambiguationData":[TD([[makeQuery(id+"F7.imprint","IMPRINT",EDGE,{"derivedFrom":sQuery(id+"F7.wireOp",EDGE,"E12.6.5.0")}),-1.0]])]});
            var Q98;
            Q98=makeQuery(id+"F7.imprint","IMPRINT",FACE,{"disambiguationData":[TD([[makeQuery(id+"F7.imprint","IMPRINT",EDGE,{"derivedFrom":sQuery(id+"F7.wireOp",EDGE,"E12.6.4.0")}),-1.0]])]});
            var Q99;
            Q99=makeQuery(id+"F7.imprint","IMPRINT",FACE,{"disambiguationData":[TD([[makeQuery(id+"F7.imprint","IMPRINT",EDGE,{"derivedFrom":sQuery(id+"F7.wireOp",EDGE,"E12.6.3.0")}),-1.0]])]});
            var Q100;
            Q100=makeQuery(id+"F7.imprint","IMPRINT",FACE,{"disambiguationData":[TD([[makeQuery(id+"F7.imprint","IMPRINT",EDGE,{"derivedFrom":sQuery(id+"F7.wireOp",EDGE,"E12.7.3.0")}),-1.0]])]});
            var Q101;
            Q101=makeQuery(id+"F7.imprint","IMPRINT",FACE,{"disambiguationData":[TD([[makeQuery(id+"F7.imprint","IMPRINT",EDGE,{"derivedFrom":sQuery(id+"F7.wireOp",EDGE,"E12.7.4.0")}),-1.0]])]});
            var Q102;
            Q102=makeQuery(id+"F7.imprint","IMPRINT",FACE,{"disambiguationData":[TD([[makeQuery(id+"F7.imprint","IMPRINT",EDGE,{"derivedFrom":sQuery(id+"F7.wireOp",EDGE,"E12.7.5.0")}),-1.0]])]});
            var Q103;
            Q103=makeQuery(id+"F7.imprint","IMPRINT",FACE,{"disambiguationData":[TD([[makeQuery(id+"F7.imprint","IMPRINT",EDGE,{"derivedFrom":sQuery(id+"F7.wireOp",EDGE,"E12.7.6.0")}),-1.0]])]});
            var Q104;
            Q104=makeQuery(id+"F7.imprint","IMPRINT",FACE,{"disambiguationData":[TD([[makeQuery(id+"F7.imprint","IMPRINT",EDGE,{"derivedFrom":sQuery(id+"F7.wireOp",EDGE,"E12.7.7.0")}),-1.0]])]});
            var Q105;
            Q105=makeQuery(id+"F7.imprint","IMPRINT",FACE,{"disambiguationData":[TD([[makeQuery(id+"F7.imprint","IMPRINT",EDGE,{"derivedFrom":sQuery(id+"F7.wireOp",EDGE,"E12.7.8.0")}),-1.0]])]});
            var Q106;
            Q106=makeQuery(id+"F7.imprint","IMPRINT",FACE,{"disambiguationData":[TD([[makeQuery(id+"F7.imprint","IMPRINT",EDGE,{"derivedFrom":sQuery(id+"F7.wireOp",EDGE,"E12.7.9.1")}),-1.0]])]});
            var Q107;
            Q107=makeQuery(id+"F7.imprint","IMPRINT",FACE,{"disambiguationData":[TD([[makeQuery(id+"F7.imprint","IMPRINT",EDGE,{"derivedFrom":sQuery(id+"F7.wireOp",EDGE,"E13.7.1.0")}),-1.0]])]});
            var Q108;
            Q108=makeQuery(id+"F7.imprint","IMPRINT",FACE,{"disambiguationData":[TD([[makeQuery(id+"F7.imprint","IMPRINT",EDGE,{"derivedFrom":sQuery(id+"F7.wireOp",EDGE,"E13.7.2.0")}),-1.0]])]});
            var Q109;
            Q109=makeQuery(id+"F7.imprint","IMPRINT",FACE,{"disambiguationData":[TD([[makeQuery(id+"F7.imprint","IMPRINT",EDGE,{"derivedFrom":sQuery(id+"F7.wireOp",EDGE,"E13.7.3.0")}),-1.0]])]});
            var Q110;
            Q110=makeQuery(id+"F7.imprint","IMPRINT",FACE,{"disambiguationData":[TD([[makeQuery(id+"F7.imprint","IMPRINT",EDGE,{"derivedFrom":sQuery(id+"F7.wireOp",EDGE,"E12.8.3.0")}),-1.0]])]});
            var Q111;
            Q111=makeQuery(id+"F7.imprint","IMPRINT",FACE,{"disambiguationData":[TD([[makeQuery(id+"F7.imprint","IMPRINT",EDGE,{"derivedFrom":sQuery(id+"F7.wireOp",EDGE,"E12.8.4.0")}),-1.0]])]});
            var Q112;
            Q112=makeQuery(id+"F7.imprint","IMPRINT",FACE,{"disambiguationData":[TD([[makeQuery(id+"F7.imprint","IMPRINT",EDGE,{"derivedFrom":sQuery(id+"F7.wireOp",EDGE,"E12.9.3.0")}),-1.0]])]});
            var Q113;
            Q113=makeQuery(id+"F7.imprint","IMPRINT",FACE,{"disambiguationData":[TD([[makeQuery(id+"F7.imprint","IMPRINT",EDGE,{"derivedFrom":sQuery(id+"F7.wireOp",EDGE,"E12.9.4.0")}),-1.0]])]});
            var Q114;
            Q114=makeQuery(id+"F7.imprint","IMPRINT",FACE,{"disambiguationData":[TD([[makeQuery(id+"F7.imprint","IMPRINT",EDGE,{"derivedFrom":sQuery(id+"F7.wireOp",EDGE,"E12.9.5.0")}),-1.0]])]});
            var Q115;
            Q115=makeQuery(id+"F7.imprint","IMPRINT",FACE,{"disambiguationData":[TD([[makeQuery(id+"F7.imprint","IMPRINT",EDGE,{"derivedFrom":sQuery(id+"F7.wireOp",EDGE,"E12.8.5.0")}),-1.0]])]});
            var Q116;
            Q116=makeQuery(id+"F7.imprint","IMPRINT",FACE,{"disambiguationData":[TD([[makeQuery(id+"F7.imprint","IMPRINT",EDGE,{"derivedFrom":sQuery(id+"F7.wireOp",EDGE,"E12.8.6.0")}),-1.0]])]});
            var Q117;
            Q117=makeQuery(id+"F7.imprint","IMPRINT",FACE,{"disambiguationData":[TD([[makeQuery(id+"F7.imprint","IMPRINT",EDGE,{"derivedFrom":sQuery(id+"F7.wireOp",EDGE,"E12.9.6.0")}),-1.0]])]});
            var Q118;
            Q118=makeQuery(id+"F7.imprint","IMPRINT",FACE,{"disambiguationData":[TD([[makeQuery(id+"F7.imprint","IMPRINT",EDGE,{"derivedFrom":sQuery(id+"F7.wireOp",EDGE,"E12.9.7.0")}),-1.0]])]});
            var Q119;
            Q119=makeQuery(id+"F7.imprint","IMPRINT",FACE,{"disambiguationData":[TD([[makeQuery(id+"F7.imprint","IMPRINT",EDGE,{"derivedFrom":sQuery(id+"F7.wireOp",EDGE,"E12.8.7.0")}),-1.0]])]});
            var Q120;
            Q120=makeQuery(id+"F7.imprint","IMPRINT",FACE,{"disambiguationData":[TD([[makeQuery(id+"F7.imprint","IMPRINT",EDGE,{"derivedFrom":sQuery(id+"F7.wireOp",EDGE,"E12.8.8.0")}),-1.0]])]});
            var Q121;
            Q121=makeQuery(id+"F7.imprint","IMPRINT",FACE,{"disambiguationData":[TD([[makeQuery(id+"F7.imprint","IMPRINT",EDGE,{"derivedFrom":sQuery(id+"F7.wireOp",EDGE,"E12.9.8.0")}),-1.0]])]});
            var Q122;
            Q122=makeQuery(id+"F7.imprint","IMPRINT",FACE,{"disambiguationData":[TD([[makeQuery(id+"F7.imprint","IMPRINT",EDGE,{"derivedFrom":sQuery(id+"F7.wireOp",EDGE,"E12.9.9.1")}),-1.0]])]});
            var Q123;
            Q123=makeQuery(id+"F7.imprint","IMPRINT",FACE,{"disambiguationData":[TD([[makeQuery(id+"F7.imprint","IMPRINT",EDGE,{"derivedFrom":sQuery(id+"F7.wireOp",EDGE,"E12.8.9.1")}),-1.0]])]});
            var Q124;
            Q124=makeQuery(id+"F7.imprint","IMPRINT",FACE,{"disambiguationData":[TD([[makeQuery(id+"F7.imprint","IMPRINT",EDGE,{"derivedFrom":sQuery(id+"F7.wireOp",EDGE,"E13.8.1.0")}),-1.0]])]});
            var Q125;
            Q125=makeQuery(id+"F7.imprint","IMPRINT",FACE,{"disambiguationData":[TD([[makeQuery(id+"F7.imprint","IMPRINT",EDGE,{"derivedFrom":sQuery(id+"F7.wireOp",EDGE,"E13.9.1.0")}),-1.0]])]});
            var Q126;
            Q126=makeQuery(id+"F7.imprint","IMPRINT",FACE,{"disambiguationData":[TD([[makeQuery(id+"F7.imprint","IMPRINT",EDGE,{"derivedFrom":sQuery(id+"F7.wireOp",EDGE,"E13.9.2.0")}),-1.0]])]});
            var Q127;
            Q127=makeQuery(id+"F7.imprint","IMPRINT",FACE,{"disambiguationData":[TD([[makeQuery(id+"F7.imprint","IMPRINT",EDGE,{"derivedFrom":sQuery(id+"F7.wireOp",EDGE,"E13.8.2.0")}),-1.0]])]});
            var Q128;
            Q128=makeQuery(id+"F7.imprint","IMPRINT",FACE,{"disambiguationData":[TD([[makeQuery(id+"F7.imprint","IMPRINT",EDGE,{"derivedFrom":sQuery(id+"F7.wireOp",EDGE,"E13.8.3.0")}),-1.0]])]});
            var Q129;
            Q129=makeQuery(id+"F7.imprint","IMPRINT",FACE,{"disambiguationData":[TD([[makeQuery(id+"F7.imprint","IMPRINT",EDGE,{"derivedFrom":sQuery(id+"F7.wireOp",EDGE,"E13.9.3.0")}),-1.0]])]});
            extrude(context, id + "F8", {"entities" : qUnion([Q0, Q1, Q2, Q3, Q4, Q5, Q6, Q7, Q8, Q9, Q10, Q11, Q12, Q13, Q14, Q15, Q16, Q17, Q18, Q19, Q20, Q21, Q22, Q23, Q24, Q25, Q26, Q27, Q28, Q29, Q30, Q31, Q32, Q33, Q34, Q35, Q36, Q37, Q38, Q39, Q40, Q41, Q42, Q43, Q44, Q45, Q46, Q47, Q48, Q49, Q50, Q51, Q52, Q53, Q54, Q55, Q56, Q57, Q58, Q59, Q60, Q61, Q62, Q63, Q64, Q65, Q66, Q67, Q68, Q69, Q70, Q71, Q72, Q73, Q74, Q75, Q76, Q77, Q78, Q79, Q80, Q81, Q82, Q83, Q84, Q85, Q86, Q87, Q88, Q89, Q90, Q91, Q92, Q93, Q94, Q95, Q96, Q97, Q98, Q99, Q100, Q101, Q102, Q103, Q104, Q105, Q106, Q107, Q108, Q109, Q110, Q111, Q112, Q113, Q114, Q115, Q116, Q117, Q118, Q119, Q120, Q121, Q122, Q123, Q124, Q125, Q126, Q127, Q128, Q129]), "operationType" : NewBodyOperationType.REMOVE, "endBound" : BoundingType.SYMMETRIC, "depth" : 20000 * mm, "offsetDistance" : 25 * mm});
        }
    });
